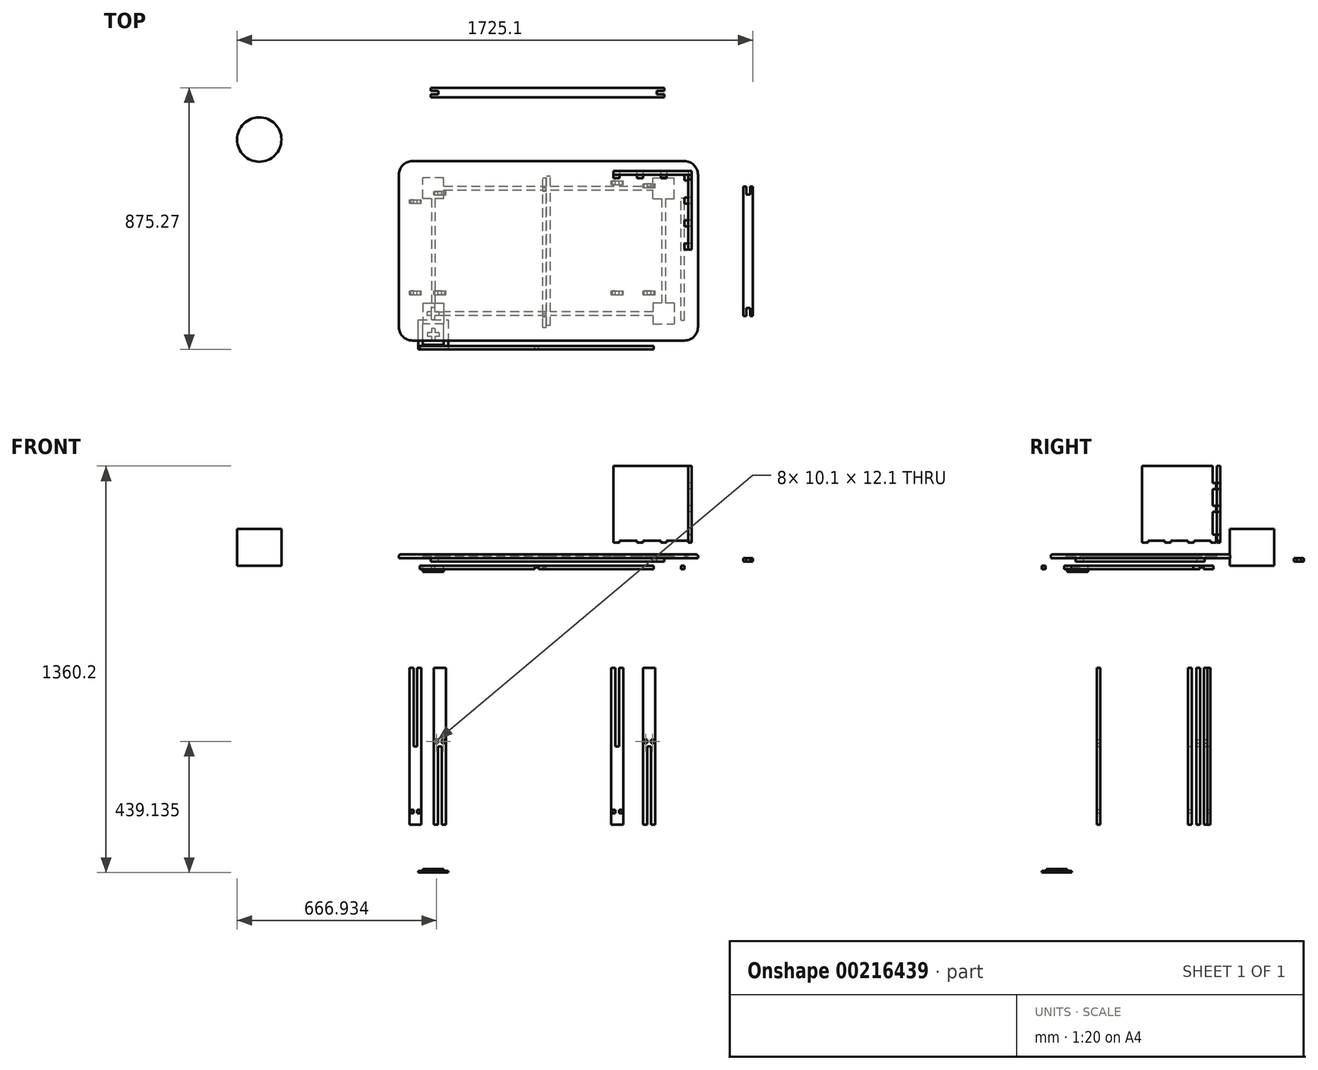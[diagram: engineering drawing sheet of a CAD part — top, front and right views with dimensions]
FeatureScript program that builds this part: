
annotation { "Feature Type Name" : "Feature", "Feature Type Description" : "" }
export const myFeature = defineFeature(function(context is Context, id is Id, definition is map)
    precondition{}
    {
        {
            var Q0;
            Q0=qCreatedBy(makeId("Top.planeOp"),FACE);
            var sketch = newSketch(context, id + "F0", { "sketchPlane" : qUnion([Q0])});
            skLineSegment(sketch, "E0.bottom", {"start": v(-704.37, 434.25) * mm, "end": v(295.63, 434.25) * mm});
            skLineSegment(sketch, "E0.top", {"start": v(-704.37, -165.75) * mm, "end": v(295.63, -165.75) * mm});
            skLineSegment(sketch, "E0.left", {"start": v(-704.37, 434.25) * mm, "end": v(-704.37, -165.75) * mm});
            skLineSegment(sketch, "E0.right", {"start": v(295.63, 434.25) * mm, "end": v(295.63, -165.75) * mm});
            skSolve(sketch);
        }
        {
            var Q0;
            Q0=makeQuery(id+"F0.imprint","IMPRINT",FACE,{"disambiguationData":[TD([[makeQuery(id+"F0.imprint","IMPRINT",EDGE,{"derivedFrom":sQuery(id+"F0.wireOp",EDGE,"E0.bottom")}),-1.0]])]});
            extrude(context, id + "F1", {"entities" : qUnion([Q0]), "depth" : 12 * mm});
        }
        {
            var Q0;
            Q0=makeQuery(id+"F1.opExtrude","CAP_EDGE",EDGE,{"disambiguationData":[OSD([sQuery(id+"F0.wireOp",EDGE,"E0.top")])],"isStart":false});
            var Q1;
            Q1=makeQuery(id+"F1.opExtrude","CAP_EDGE",EDGE,{"disambiguationData":[OSD([sQuery(id+"F0.wireOp",EDGE,"E0.left")])],"isStart":false});
            var Q2;
            Q2=makeQuery(id+"F1.opExtrude","CAP_FACE",FACE,{"disambiguationData":[OSD([sQuery(id+"F0.wireOp",EDGE,"E0.bottom"),sQuery(id+"F0.wireOp",EDGE,"E0.top"),sQuery(id+"F0.wireOp",EDGE,"E0.left"),sQuery(id+"F0.wireOp",EDGE,"E0.right")])],"isStart":false});
            fillet(context, id + "F2", {"entities" : qUnion([Q0, Q1, Q2]), "radius" : 5 * mm, "tangentPropagation" : true, "allowEdgeOverflow" : false});
        }
        {
            var Q0;
            Q0=makeQuery(id+"F1.opExtrude","CAP_FACE",FACE,{"disambiguationData":[OSD([sQuery(id+"F0.wireOp",EDGE,"E0.bottom"),sQuery(id+"F0.wireOp",EDGE,"E0.top"),sQuery(id+"F0.wireOp",EDGE,"E0.left"),sQuery(id+"F0.wireOp",EDGE,"E0.right")])],"isStart":true});
            var sketch = newSketch(context, id + "F3", { "sketchPlane" : qUnion([Q0])});
            skLineSegment(sketch, "E1.0", {"start": v(-704.37, -434.25) * mm, "end": v(-704.37, -134.25) * mm});
            skLineSegment(sketch, "E2.0", {"start": v(-704.37, 165.75) * mm, "end": v(295.63, 165.75) * mm});
            skLineSegment(sketch, "E3.0", {"start": v(-704.37, -434.25) * mm, "end": v(295.63, -434.25) * mm});
            skLineSegment(sketch, "E4.0", {"start": v(295.63, -134.25) * mm, "end": v(295.63, 165.75) * mm});
            skPoint(sketch, "E5", {"position": v(-704.37, -134.25) * mm});
            skPoint(sketch, "E6", {"position": v(295.63, -134.25) * mm});
            skPoint(sketch, "E7.orphan", {"position": v(295.63, -434.25) * mm});
            skPoint(sketch, "E8", {"position": v(-704.37, -284.25) * mm});
            skPoint(sketch, "E9", {"position": v(295.63, 15.75) * mm});
            skLineSegment(sketch, "E10", {"start": v(-704.37, -134.25) * mm, "end": v(-704.37, 165.75) * mm});
            skLineSegment(sketch, "E11", {"start": v(295.63, -134.25) * mm, "end": v(295.63, -434.25) * mm});
            skPoint(sketch, "E12", {"position": v(-704.37, 15.75) * mm});
            skPoint(sketch, "E13", {"position": v(295.63, -284.25) * mm});
            skPoint(sketch, "E14", {"position": v(-554.37, 40.75) * mm});
            skPoint(sketch, "E15", {"position": v(-554.37, -309.25) * mm});
            skLineSegment(sketch, "E16", {"start": v(-204.37, 15.75) * mm, "end": v(-204.37, -279) * mm, "construction": true});
            skPoint(sketch, "E17.MirrorP", {"position": v(145.63, 40.75) * mm});
            skPoint(sketch, "E18.MirrorP", {"position": v(145.63, -309.25) * mm});
            skLineSegment(sketch, "E19.bottom", {"start": v(-554.37, -309.25) * mm, "end": v(-624.37, -309.25) * mm});
            skLineSegment(sketch, "E19.top", {"start": v(-554.37, -379.25) * mm, "end": v(-624.37, -379.25) * mm});
            skLineSegment(sketch, "E19.left", {"start": v(-554.37, -309.25) * mm, "end": v(-554.37, -379.25) * mm});
            skLineSegment(sketch, "E19.right", {"start": v(-624.37, -309.25) * mm, "end": v(-624.37, -379.25) * mm});
            skLineSegment(sketch, "E20.top", {"start": v(-554.37, 110.75) * mm, "end": v(-624.37, 110.75) * mm});
            skLineSegment(sketch, "E20.left", {"start": v(-554.37, 40.75) * mm, "end": v(-554.37, 110.75) * mm});
            skLineSegment(sketch, "E20.right", {"start": v(-624.37, 40.75) * mm, "end": v(-624.37, 110.75) * mm});
            skLineSegment(sketch, "E21.MirrorCS", {"start": v(145.63, 40.75) * mm, "end": v(145.63, 110.75) * mm});
            skLineSegment(sketch, "E22.MirrorCS", {"start": v(145.63, 110.75) * mm, "end": v(215.63, 110.75) * mm});
            skLineSegment(sketch, "E23.MirrorCS", {"start": v(215.63, 40.75) * mm, "end": v(215.63, 110.75) * mm});
            skLineSegment(sketch, "E24", {"start": v(-624.37, 40.75) * mm, "end": v(-554.37, 40.75) * mm});
            skLineSegment(sketch, "E25.MirrorCS", {"start": v(215.63, 40.75) * mm, "end": v(145.63, 40.75) * mm});
            skLineSegment(sketch, "E26.MirrorCS", {"start": v(215.63, -309.25) * mm, "end": v(215.63, -379.25) * mm});
            skLineSegment(sketch, "E27.MirrorCS", {"start": v(145.63, -309.25) * mm, "end": v(145.63, -379.25) * mm});
            skLineSegment(sketch, "E28.MirrorCS", {"start": v(145.63, -379.25) * mm, "end": v(215.63, -379.25) * mm});
            skPoint(sketch, "E29.MirrorCS.start.orphan", {"position": v(215.63, -309.25) * mm});
            skLineSegment(sketch, "E30", {"start": v(145.63, -309.25) * mm, "end": v(215.63, -309.25) * mm});
            skSolve(sketch);
        }
        {
            var Q0;
            Q0=makeQuery(id+"F3.imprint","IMPRINT",FACE,{"disambiguationData":[TD([[makeQuery(id+"F3.imprint","IMPRINT",EDGE,{"derivedFrom":sQuery(id+"F3.wireOp",EDGE,"E20.top")}),1.0]])]});
            var Q1;
            Q1=makeQuery(id+"F3.imprint","IMPRINT",FACE,{"disambiguationData":[TD([[makeQuery(id+"F3.imprint","IMPRINT",EDGE,{"derivedFrom":sQuery(id+"F3.wireOp",EDGE,"E19.bottom")}),1.0]])]});
            var Q2;
            Q2=makeQuery(id+"F3.imprint","IMPRINT",FACE,{"disambiguationData":[TD([[makeQuery(id+"F3.imprint","IMPRINT",EDGE,{"derivedFrom":sQuery(id+"F3.wireOp",EDGE,"E26.MirrorCS")}),-1.0]])]});
            var Q3;
            Q3=makeQuery(id+"F3.imprint","IMPRINT",FACE,{"disambiguationData":[TD([[makeQuery(id+"F3.imprint","IMPRINT",EDGE,{"derivedFrom":sQuery(id+"F3.wireOp",EDGE,"E21.MirrorCS")}),-1.0]])]});
            extrude(context, id + "F4", {"entities" : qUnion([Q0, Q1, Q2, Q3]), "operationType" : NewBodyOperationType.REMOVE, "oppositeDirection" : true, "depth" : 6 * mm});
        }
        {
            var Q0;
            Q0=makeQuery(id+"F1.opExtrude","CAP_FACE",FACE,{"disambiguationData":[OSD([sQuery(id+"F0.wireOp",EDGE,"E0.bottom"),sQuery(id+"F0.wireOp",EDGE,"E0.top"),sQuery(id+"F0.wireOp",EDGE,"E0.left"),sQuery(id+"F0.wireOp",EDGE,"E0.right")])],"isStart":true});
            cPlane(context, id + "F5", {"entities" : qUnion([Q0]), "cplaneType" : CPlaneType.OFFSET, "offset" : 25 * mm, "width" : 150 * mm, "height" : 150 * mm});
        }
        {
            var Q0;
            Q0=qCreatedBy(id+"F5.planeOp",FACE);
            var sketch = newSketch(context, id + "F6", { "sketchPlane" : qUnion([Q0])});
            skLineSegment(sketch, "E31.0", {"start": v(-554.37, 40.75) * mm, "end": v(-554.37, 110.75) * mm});
            skLineSegment(sketch, "E32.0", {"start": v(-554.37, 110.75) * mm, "end": v(-624.37, 110.75) * mm});
            skLineSegment(sketch, "E33.0", {"start": v(-624.37, 40.75) * mm, "end": v(-624.37, 110.75) * mm});
            skLineSegment(sketch, "E34.0", {"start": v(-624.37, 40.75) * mm, "end": v(-554.37, 40.75) * mm});
            skPoint(sketch, "E35", {"position": v(-554.37, 75.75) * mm});
            skPoint(sketch, "E36", {"position": v(-589.37, 40.75) * mm});
            skPoint(sketch, "E37", {"position": v(-589.37, 75.75) * mm});
            skLineSegment(sketch, "E38", {"start": v(-599.37, 75.75) * mm, "end": v(-579.37, 75.75) * mm});
            skSolve(sketch);
        }
        {
            var Q0;
            Q0=makeQuery(id+"F6.imprint","IMPRINT",FACE,{"disambiguationData":[TD([[makeQuery(id+"F6.imprint","IMPRINT",EDGE,{"derivedFrom":sQuery(id+"F6.wireOp",EDGE,"E31.0")}),1.0]])]});
            extrude(context, id + "F7", {"entities" : qUnion([Q0]), "depth" : 20.8 * mm});
        }
        {
            var Q0;
            Q0=makeQuery(id+"F7.opExtrude","CAP_FACE",FACE,{"disambiguationData":[OSD([sQuery(id+"F6.wireOp",EDGE,"E31.0"),sQuery(id+"F6.wireOp",EDGE,"E32.0"),sQuery(id+"F6.wireOp",EDGE,"E33.0"),sQuery(id+"F6.wireOp",EDGE,"E34.0")])],"isStart":true});
            var sketch = newSketch(context, id + "F8", { "sketchPlane" : qUnion([Q0])});
            skPoint(sketch, "E39", {"position": v(-589.37, -40.75) * mm});
            skPoint(sketch, "E40", {"position": v(-554.37, -75.75) * mm});
            skPoint(sketch, "E41", {"position": v(-589.37, -75.75) * mm});
            skLineSegment(sketch, "E42", {"start": v(-589.37, -75.75) * mm, "end": v(-583.37, -75.75) * mm, "construction": true});
            skLineSegment(sketch, "E43.bottom", {"start": v(-583.37, -69.75) * mm, "end": v(-554.37, -69.75) * mm});
            skLineSegment(sketch, "E43.top", {"start": v(-583.37, -81.75) * mm, "end": v(-554.37, -81.75) * mm});
            skLineSegment(sketch, "E43.left", {"start": v(-589.37, -69.75) * mm, "end": v(-589.37, -81.75) * mm, "construction": true});
            skLineSegment(sketch, "E43.right", {"start": v(-554.37, -69.75) * mm, "end": v(-554.37, -81.75) * mm});
            skLineSegment(sketch, "E44.right", {"start": v(-624.37, -69.75) * mm, "end": v(-624.37, -81.75) * mm});
            skLineSegment(sketch, "E45.bottom", {"start": v(-595.37, -75.75) * mm, "end": v(-583.37, -75.75) * mm, "construction": true});
            skLineSegment(sketch, "E45.top", {"start": v(-595.37, -40.75) * mm, "end": v(-583.37, -40.75) * mm});
            skLineSegment(sketch, "E45.left", {"start": v(-595.37, -69.75) * mm, "end": v(-595.37, -40.75) * mm});
            skLineSegment(sketch, "E45.right", {"start": v(-583.37, -69.75) * mm, "end": v(-583.37, -40.75) * mm});
            skLineSegment(sketch, "E46.bottom", {"start": v(-583.37, -75.75) * mm, "end": v(-595.37, -75.75) * mm, "construction": true});
            skLineSegment(sketch, "E46.top", {"start": v(-583.37, -110.75) * mm, "end": v(-595.37, -110.75) * mm});
            skPoint(sketch, "E47.end.orphan", {"position": v(-589.37, -81.75) * mm});
            skLineSegment(sketch, "E48", {"start": v(-583.37, -81.75) * mm, "end": v(-595.37, -81.75) * mm});
            skLineSegment(sketch, "E49", {"start": v(-595.37, -69.75) * mm, "end": v(-595.37, -81.75) * mm});
            skSolve(sketch);
        }
        {
            var Q0;
            Q0=makeQuery(id+"F8.imprint","IMPRINT",FACE,{"disambiguationData":[TD([[makeQuery(id+"F8.imprint","IMPRINT",EDGE,{"derivedFrom":sQuery(id+"F8.wireOp",EDGE,"E43.bottom")}),-1.0]])]});
            extrude(context, id + "F9", {"entities" : qUnion([Q0]), "operationType" : NewBodyOperationType.REMOVE, "oppositeDirection" : true, "depth" : 12 * mm});
        }
        {
            var Q0;
            Q0=qCreatedBy(makeId("Front.planeOp"),FACE);
            var sketch = newSketch(context, id + "F10", { "sketchPlane" : qUnion([Q0])});
            skLineSegment(sketch, "E50.bottom", {"start": v(-669.23, -367.02) * mm, "end": v(-629.23, -367.02) * mm});
            skLineSegment(sketch, "E50.top", {"start": v(-669.23, -892.02) * mm, "end": v(-629.23, -892.02) * mm});
            skLineSegment(sketch, "E50.left", {"start": v(-669.23, -367.02) * mm, "end": v(-669.23, -892.02) * mm});
            skLineSegment(sketch, "E50.right", {"start": v(-629.23, -367.02) * mm, "end": v(-629.23, -892.02) * mm});
            skLineSegment(sketch, "E51.bottom", {"start": v(-587.48, -367.02) * mm, "end": v(-547.48, -367.02) * mm});
            skLineSegment(sketch, "E51.top", {"start": v(-587.48, -892.02) * mm, "end": v(-547.48, -892.02) * mm});
            skLineSegment(sketch, "E51.left", {"start": v(-587.48, -367.02) * mm, "end": v(-587.48, -892.02) * mm});
            skLineSegment(sketch, "E51.right", {"start": v(-547.48, -367.02) * mm, "end": v(-547.48, -892.02) * mm});
            skPoint(sketch, "E52", {"position": v(-655.28, -367.02) * mm});
            skPoint(sketch, "E53", {"position": v(-643.18, -367.02) * mm});
            skLineSegment(sketch, "E54.bottom", {"start": v(-655.28, -367.02) * mm, "end": v(-643.18, -367.02) * mm});
            skLineSegment(sketch, "E54.top", {"start": v(-655.28, -629.52) * mm, "end": v(-643.18, -629.52) * mm});
            skLineSegment(sketch, "E54.left", {"start": v(-655.28, -367.02) * mm, "end": v(-655.28, -629.52) * mm});
            skLineSegment(sketch, "E54.right", {"start": v(-643.18, -367.02) * mm, "end": v(-643.18, -629.52) * mm});
            skPoint(sketch, "E55", {"position": v(-573.53, -892.02) * mm});
            skPoint(sketch, "E56", {"position": v(-561.43, -892.02) * mm});
            skPoint(sketch, "E57.oppositeSnap0", {"position": v(-629.23, -629.52) * mm});
            skLineSegment(sketch, "E57.bottom", {"start": v(-561.43, -892.02) * mm, "end": v(-573.53, -892.02) * mm});
            skLineSegment(sketch, "E57.top", {"start": v(-561.43, -629.52) * mm, "end": v(-573.53, -629.52) * mm});
            skLineSegment(sketch, "E57.left", {"start": v(-561.43, -892.02) * mm, "end": v(-561.43, -629.52) * mm});
            skLineSegment(sketch, "E57.right", {"start": v(-573.53, -892.02) * mm, "end": v(-573.53, -629.52) * mm});
            skLineSegment(sketch, "E58", {"start": v(-567.48, -629.52) * mm, "end": v(-567.48, -367.02) * mm, "construction": true});
            skLineSegment(sketch, "E59", {"start": v(-649.23, -629.52) * mm, "end": v(-649.23, -892.02) * mm, "construction": true});
            skSolve(sketch);
        }
        {
            var Q0;
            Q0=makeQuery(id+"F7.opExtrude","CAP_FACE",FACE,{"disambiguationData":[OSD([sQuery(id+"F6.wireOp",EDGE,"E31.0"),sQuery(id+"F6.wireOp",EDGE,"E32.0"),sQuery(id+"F6.wireOp",EDGE,"E33.0"),sQuery(id+"F6.wireOp",EDGE,"E34.0")])],"isStart":false});
            var sketch = newSketch(context, id + "F11", { "sketchPlane" : qUnion([Q0])});
            skLineSegment(sketch, "E60.0.0", {"start": v(-624.37, 110.75) * mm, "end": v(-624.37, 40.75) * mm});
            skLineSegment(sketch, "E60.0.1", {"start": v(-624.37, 40.75) * mm, "end": v(-554.37, 40.75) * mm});
            skLineSegment(sketch, "E60.0.2", {"start": v(-554.37, 40.75) * mm, "end": v(-554.37, 110.75) * mm});
            skLineSegment(sketch, "E60.0.3", {"start": v(-554.37, 110.75) * mm, "end": v(-624.37, 110.75) * mm});
            skPoint(sketch, "E61", {"position": v(-569.37, 110.75) * mm});
            skPoint(sketch, "E62", {"position": v(-609.37, 110.75) * mm});
            skPoint(sketch, "E63", {"position": v(-554.37, 95.75) * mm});
            skPoint(sketch, "E64", {"position": v(-554.37, 55.75) * mm});
            skLineSegment(sketch, "E65.bottom", {"start": v(-583.27, 95.75) * mm, "end": v(-595.47, 95.75) * mm});
            skLineSegment(sketch, "E65.top", {"start": v(-583.27, 55.75) * mm, "end": v(-595.47, 55.75) * mm});
            skLineSegment(sketch, "E65.left", {"start": v(-554.37, 95.75) * mm, "end": v(-554.37, 55.75) * mm});
            skLineSegment(sketch, "E65.right", {"start": v(-609.37, 81.85) * mm, "end": v(-609.37, 69.65) * mm});
            skLineSegment(sketch, "E66.bottom", {"start": v(-569.37, 110.75) * mm, "end": v(-609.37, 110.75) * mm});
            skLineSegment(sketch, "E66.left", {"start": v(-569.37, 81.85) * mm, "end": v(-569.37, 69.65) * mm});
            skPoint(sketch, "E67", {"position": v(-554.37, 81.85) * mm});
            skPoint(sketch, "E68", {"position": v(-554.37, 69.65) * mm});
            skLineSegment(sketch, "E69.bottom", {"start": v(-569.37, 81.85) * mm, "end": v(-583.27, 81.85) * mm});
            skLineSegment(sketch, "E69.top", {"start": v(-569.37, 69.65) * mm, "end": v(-583.27, 69.65) * mm});
            skPoint(sketch, "E70", {"position": v(-583.27, 110.75) * mm});
            skPoint(sketch, "E71", {"position": v(-595.47, 110.75) * mm});
            skLineSegment(sketch, "E72.bottom", {"start": v(-595.47, 95.75) * mm, "end": v(-583.27, 95.75) * mm});
            skLineSegment(sketch, "E72.top", {"start": v(-595.47, 55.75) * mm, "end": v(-583.27, 55.75) * mm});
            skLineSegment(sketch, "E72.left", {"start": v(-595.47, 95.75) * mm, "end": v(-595.47, 81.85) * mm});
            skLineSegment(sketch, "E72.right", {"start": v(-583.27, 95.75) * mm, "end": v(-583.27, 81.85) * mm});
            skPoint(sketch, "E73.orphan", {"position": v(-609.37, 55.75) * mm});
            skLineSegment(sketch, "E74.trimOffspring", {"start": v(-595.47, 81.85) * mm, "end": v(-609.37, 81.85) * mm});
            skLineSegment(sketch, "E75.trimOffspring", {"start": v(-595.47, 69.65) * mm, "end": v(-595.47, 55.75) * mm});
            skLineSegment(sketch, "E76.trimOffspring", {"start": v(-583.27, 69.65) * mm, "end": v(-583.27, 55.75) * mm});
            skLineSegment(sketch, "E77.trimOffspring", {"start": v(-595.47, 69.65) * mm, "end": v(-609.37, 69.65) * mm});
            skSolve(sketch);
        }
        {
            var Q0;
            {var subQ5=sQuery(id+"F11.wireOp",EDGE,"E72.bottom");Q0=makeQuery(id+"F11.imprint","IMPRINT",FACE,{"disambiguationData":[TD([[makeQuery(id+"F11.imprint","IMPRINT",EDGE,{"derivedFrom":subQ5}),-1.0]])]});}
            var Q1;
            {var subQ0=sQuery(id+"F11.wireOp",EDGE,"E72.right");var subQ1=sQuery(id+"F11.wireOp",EDGE,"E69.bottom");var subQ2=makeQuery(id+"F11.imprint","INTERSECT",VERTEX,{"derivedFrom":[subQ1,subQ0]});Q1=makeQuery(id+"F11.imprint","IMPRINT",FACE,{"disambiguationData":[TD([[makeQuery(id+"F11.imprint","IMPRINT",EDGE,{"disambiguationData":[TD([[subQ2,-1.0]])],"derivedFrom":subQ1}),1.0]])]});}
            var Q2;
            {var subQ0=sQuery(id+"F11.wireOp",EDGE,"E65.right");Q2=makeQuery(id+"F11.imprint","IMPRINT",FACE,{"disambiguationData":[TD([[makeQuery(id+"F11.imprint","IMPRINT",EDGE,{"derivedFrom":subQ0}),1.0]])]});}
            var Q3;
            {var subQ0=sQuery(id+"F11.wireOp",EDGE,"E66.left");Q3=makeQuery(id+"F11.imprint","IMPRINT",FACE,{"disambiguationData":[TD([[makeQuery(id+"F11.imprint","IMPRINT",EDGE,{"derivedFrom":subQ0}),-1.0]])]});}
            var Q4;
            {var subQ5=sQuery(id+"F11.wireOp",EDGE,"E72.top");Q4=makeQuery(id+"F11.imprint","IMPRINT",FACE,{"disambiguationData":[TD([[makeQuery(id+"F11.imprint","IMPRINT",EDGE,{"derivedFrom":subQ5}),1.0]])]});}
            extrude(context, id + "F12", {"entities" : qUnion([Q0, Q1, Q2, Q3, Q4]), "operationType" : NewBodyOperationType.REMOVE, "oppositeDirection" : true, "depth" : 8 * mm});
        }
        {
            var Q0;
            Q0=makeQuery(id+"F10.imprint","IMPRINT",FACE,{"disambiguationData":[TD([[makeQuery(id+"F10.imprint","IMPRINT",EDGE,{"derivedFrom":sQuery(id+"F10.wireOp",EDGE,"E50.top")}),1.0]])]});
            var Q1;
            Q1=makeQuery(id+"F10.imprint","IMPRINT",FACE,{"disambiguationData":[TD([[makeQuery(id+"F10.imprint","IMPRINT",EDGE,{"derivedFrom":sQuery(id+"F10.wireOp",EDGE,"E51.bottom")}),-1.0]])]});
            extrude(context, id + "F13", {"entities" : qUnion([Q0, Q1]), "depth" : 12 * mm});
        }
        {
            var Q0;
            Q0=makeQuery(id+"F13.opExtrude","SWEPT_BODY",BODY,{"disambiguationData":[OSD([sQuery(id+"F10.wireOp",EDGE,"E50.bottom"),sQuery(id+"F10.wireOp",EDGE,"E50.top"),sQuery(id+"F10.wireOp",EDGE,"E50.left"),sQuery(id+"F10.wireOp",EDGE,"E50.right"),sQuery(id+"F10.wireOp",EDGE,"E54.top"),sQuery(id+"F10.wireOp",EDGE,"E54.left"),sQuery(id+"F10.wireOp",EDGE,"E54.right")])]});
            transform(context, id + "F14", {"entities" : qUnion([Q0]), "transformType" : TransformType.TRANSLATION_3D, "dx" : 675 * mm, "dy" : 0 * mm, "dz" : 0 * mm, "makeCopy" : true});
        }
        {
            var Q0;
            Q0=makeQuery(id+"F13.opExtrude","SWEPT_BODY",BODY,{"disambiguationData":[OSD([sQuery(id+"F10.wireOp",EDGE,"E51.bottom"),sQuery(id+"F10.wireOp",EDGE,"E51.top"),sQuery(id+"F10.wireOp",EDGE,"E51.left"),sQuery(id+"F10.wireOp",EDGE,"E51.right"),sQuery(id+"F10.wireOp",EDGE,"E57.top"),sQuery(id+"F10.wireOp",EDGE,"E57.left"),sQuery(id+"F10.wireOp",EDGE,"E57.right")])]});
            transform(context, id + "F15", {"entities" : qUnion([Q0]), "transformType" : TransformType.TRANSLATION_3D, "dx" : 700 * mm, "dy" : 0 * mm, "dz" : 0 * mm, "makeCopy" : true});
        }
        {
            var Q0;
            Q0=makeQuery(id+"F13.opExtrude","CAP_FACE",FACE,{"disambiguationData":[OSD([sQuery(id+"F10.wireOp",EDGE,"E50.bottom"),sQuery(id+"F10.wireOp",EDGE,"E50.top"),sQuery(id+"F10.wireOp",EDGE,"E50.left"),sQuery(id+"F10.wireOp",EDGE,"E50.right"),sQuery(id+"F10.wireOp",EDGE,"E54.top"),sQuery(id+"F10.wireOp",EDGE,"E54.left"),sQuery(id+"F10.wireOp",EDGE,"E54.right")])],"isStart":false});
            var sketch = newSketch(context, id + "F16", { "sketchPlane" : qUnion([Q0])});
            skLineSegment(sketch, "E78.0.0", {"start": v(-655.28, -367.02) * mm, "end": v(-669.23, -367.02) * mm});
            skLineSegment(sketch, "E78.0.1", {"start": v(-669.23, -367.02) * mm, "end": v(-669.23, -892.02) * mm});
            skLineSegment(sketch, "E78.0.2", {"start": v(-669.23, -892.02) * mm, "end": v(-629.23, -892.02) * mm});
            skLineSegment(sketch, "E78.0.3", {"start": v(-629.23, -892.02) * mm, "end": v(-629.23, -367.02) * mm});
            skLineSegment(sketch, "E78.0.4", {"start": v(-629.23, -367.02) * mm, "end": v(-643.18, -367.02) * mm});
            skLineSegment(sketch, "E78.0.5", {"start": v(-643.18, -367.02) * mm, "end": v(-643.18, -629.52) * mm});
            skLineSegment(sketch, "E78.0.6", {"start": v(-643.18, -629.52) * mm, "end": v(-655.28, -629.52) * mm});
            skLineSegment(sketch, "E78.0.7", {"start": v(-655.28, -629.52) * mm, "end": v(-655.28, -367.02) * mm});
            skPoint(sketch, "E79", {"position": v(-629.23, -842.02) * mm});
            skLineSegment(sketch, "E80.bottom", {"start": v(-643.18, -629.52) * mm, "end": v(-655.28, -629.52) * mm, "construction": true});
            skLineSegment(sketch, "E80.top", {"start": v(-643.18, -877.56) * mm, "end": v(-655.28, -877.56) * mm, "construction": true});
            skLineSegment(sketch, "E80.left", {"start": v(-643.18, -629.52) * mm, "end": v(-643.18, -842.02) * mm, "construction": true});
            skLineSegment(sketch, "E80.right", {"start": v(-655.28, -629.52) * mm, "end": v(-655.28, -842.02) * mm, "construction": true});
            skLineSegment(sketch, "E81.bottom", {"start": v(-643.18, -842.02) * mm, "end": v(-633.18, -842.02) * mm});
            skLineSegment(sketch, "E81.top", {"start": v(-643.18, -854.12) * mm, "end": v(-633.18, -854.12) * mm});
            skLineSegment(sketch, "E81.right", {"start": v(-633.18, -842.02) * mm, "end": v(-633.18, -854.12) * mm});
            skPoint(sketch, "E82", {"position": v(-649.23, -877.56) * mm});
            skLineSegment(sketch, "E83", {"start": v(-649.23, -877.56) * mm, "end": v(-649.23, -841.02) * mm, "construction": true});
            skLineSegment(sketch, "E84.MirrorCS", {"start": v(-655.28, -854.12) * mm, "end": v(-665.28, -854.12) * mm});
            skLineSegment(sketch, "E85.MirrorCS", {"start": v(-665.28, -842.02) * mm, "end": v(-665.28, -854.12) * mm});
            skLineSegment(sketch, "E86.MirrorCS", {"start": v(-655.28, -842.02) * mm, "end": v(-665.28, -842.02) * mm});
            skLineSegment(sketch, "E87.trimOffspring", {"start": v(-643.18, -854.12) * mm, "end": v(-643.18, -877.56) * mm, "construction": true});
            skLineSegment(sketch, "E88.trimOffspring", {"start": v(-655.28, -854.12) * mm, "end": v(-655.28, -877.56) * mm, "construction": true});
            skLineSegment(sketch, "E89", {"start": v(-643.18, -854.12) * mm, "end": v(-643.18, -842.02) * mm});
            skLineSegment(sketch, "E90", {"start": v(-655.28, -854.12) * mm, "end": v(-655.28, -842.02) * mm});
            skLineSegment(sketch, "E91.0.0", {"start": v(19.72, -367.02) * mm, "end": v(5.77, -367.02) * mm});
            skLineSegment(sketch, "E91.0.1", {"start": v(5.77, -367.02) * mm, "end": v(5.77, -892.02) * mm});
            skLineSegment(sketch, "E91.0.2", {"start": v(5.77, -892.02) * mm, "end": v(45.77, -892.02) * mm});
            skLineSegment(sketch, "E91.0.3", {"start": v(45.77, -892.02) * mm, "end": v(45.77, -367.02) * mm});
            skLineSegment(sketch, "E91.0.4", {"start": v(45.77, -367.02) * mm, "end": v(31.82, -367.02) * mm});
            skLineSegment(sketch, "E91.0.5", {"start": v(31.82, -367.02) * mm, "end": v(31.82, -629.52) * mm});
            skLineSegment(sketch, "E91.0.6", {"start": v(31.82, -629.52) * mm, "end": v(19.72, -629.52) * mm});
            skLineSegment(sketch, "E91.0.7", {"start": v(19.72, -629.52) * mm, "end": v(19.72, -367.02) * mm});
            skLineSegment(sketch, "E92", {"start": v(-629.23, -892.02) * mm, "end": v(5.77, -892.02) * mm, "construction": true});
            skPoint(sketch, "E93", {"position": v(-311.73, -892.02) * mm});
            skLineSegment(sketch, "E94", {"start": v(-311.73, -892.02) * mm, "end": v(-311.73, -731.08) * mm, "construction": true});
            skLineSegment(sketch, "E95.MirrorCS", {"start": v(19.72, -854.12) * mm, "end": v(9.72, -854.12) * mm});
            skLineSegment(sketch, "E96.MirrorCS", {"start": v(19.72, -854.12) * mm, "end": v(19.72, -842.02) * mm});
            skLineSegment(sketch, "E97.MirrorCS", {"start": v(19.72, -842.02) * mm, "end": v(9.72, -842.02) * mm});
            skLineSegment(sketch, "E98.MirrorCS", {"start": v(9.72, -842.02) * mm, "end": v(9.72, -854.12) * mm});
            skLineSegment(sketch, "E99.MirrorCS", {"start": v(31.82, -842.02) * mm, "end": v(41.82, -842.02) * mm});
            skLineSegment(sketch, "E100.MirrorCS", {"start": v(31.82, -854.12) * mm, "end": v(31.82, -842.02) * mm});
            skLineSegment(sketch, "E101.MirrorCS", {"start": v(31.82, -854.12) * mm, "end": v(41.82, -854.12) * mm});
            skLineSegment(sketch, "E102.MirrorCS", {"start": v(41.82, -842.02) * mm, "end": v(41.82, -854.12) * mm});
            skSolve(sketch);
        }
        {
            var Q0;
            Q0=makeQuery(id+"F16.imprint","IMPRINT",FACE,{"disambiguationData":[TD([[makeQuery(id+"F16.imprint","IMPRINT",EDGE,{"derivedFrom":sQuery(id+"F16.wireOp",EDGE,"E84.MirrorCS")}),-1.0]])]});
            var Q1;
            Q1=makeQuery(id+"F16.imprint","IMPRINT",FACE,{"disambiguationData":[TD([[makeQuery(id+"F16.imprint","IMPRINT",EDGE,{"derivedFrom":sQuery(id+"F16.wireOp",EDGE,"E81.bottom")}),-1.0]])]});
            var Q2;
            Q2=makeQuery(id+"F16.imprint","IMPRINT",FACE,{"disambiguationData":[TD([[makeQuery(id+"F16.imprint","IMPRINT",EDGE,{"derivedFrom":sQuery(id+"F16.wireOp",EDGE,"E95.MirrorCS")}),-1.0]])]});
            var Q3;
            Q3=makeQuery(id+"F16.imprint","IMPRINT",FACE,{"disambiguationData":[TD([[makeQuery(id+"F16.imprint","IMPRINT",EDGE,{"derivedFrom":sQuery(id+"F16.wireOp",EDGE,"E99.MirrorCS")}),-1.0]])]});
            extrude(context, id + "F17", {"entities" : qUnion([Q0, Q1, Q2, Q3]), "operationType" : NewBodyOperationType.REMOVE, "oppositeDirection" : true, "depth" : 25 * mm});
        }
        {
            var Q0;
            Q0=makeQuery(id+"F15.opPattern","COPY",FACE,{"derivedFrom":makeQuery(id+"F13.opExtrude","CAP_FACE",FACE,{"disambiguationData":[OSD([sQuery(id+"F10.wireOp",EDGE,"E51.bottom"),sQuery(id+"F10.wireOp",EDGE,"E51.top"),sQuery(id+"F10.wireOp",EDGE,"E51.left"),sQuery(id+"F10.wireOp",EDGE,"E51.right"),sQuery(id+"F10.wireOp",EDGE,"E57.top"),sQuery(id+"F10.wireOp",EDGE,"E57.left"),sQuery(id+"F10.wireOp",EDGE,"E57.right")])],"isStart":true}),"instanceName":"1"});
            var sketch = newSketch(context, id + "F18", { "sketchPlane" : qUnion([Q0])});
            skLineSegment(sketch, "E103.0.0", {"start": v(-138.57, -629.52) * mm, "end": v(-126.47, -629.52) * mm});
            skLineSegment(sketch, "E103.0.1", {"start": v(-126.47, -629.52) * mm, "end": v(-126.47, -892.02) * mm});
            skLineSegment(sketch, "E103.0.2", {"start": v(-126.47, -892.02) * mm, "end": v(-112.52, -892.02) * mm});
            skLineSegment(sketch, "E103.0.3", {"start": v(-112.52, -892.02) * mm, "end": v(-112.52, -367.02) * mm});
            skLineSegment(sketch, "E103.0.4", {"start": v(-112.52, -367.02) * mm, "end": v(-152.52, -367.02) * mm});
            skLineSegment(sketch, "E103.0.5", {"start": v(-152.52, -367.02) * mm, "end": v(-152.52, -892.02) * mm});
            skLineSegment(sketch, "E103.0.6", {"start": v(-152.52, -892.02) * mm, "end": v(-138.57, -892.02) * mm});
            skLineSegment(sketch, "E103.0.7", {"start": v(-138.57, -892.02) * mm, "end": v(-138.57, -629.52) * mm});
            skLineSegment(sketch, "E104.bottom", {"start": v(-126.47, -629.52) * mm, "end": v(-138.57, -629.52) * mm, "construction": true});
            skLineSegment(sketch, "E104.top", {"start": v(-126.47, -426.7) * mm, "end": v(-138.57, -426.7) * mm, "construction": true});
            skLineSegment(sketch, "E104.left", {"start": v(-126.47, -629.52) * mm, "end": v(-126.47, -619.12) * mm, "construction": true});
            skLineSegment(sketch, "E104.right", {"start": v(-138.57, -629.52) * mm, "end": v(-138.57, -619.12) * mm, "construction": true});
            skLineSegment(sketch, "E105.0.0", {"start": v(561.43, -629.52) * mm, "end": v(573.53, -629.52) * mm, "construction": true});
            skLineSegment(sketch, "E105.0.1", {"start": v(573.53, -629.52) * mm, "end": v(573.53, -892.02) * mm, "construction": true});
            skLineSegment(sketch, "E105.0.2", {"start": v(573.53, -892.02) * mm, "end": v(587.48, -892.02) * mm, "construction": true});
            skLineSegment(sketch, "E105.0.3", {"start": v(587.48, -892.02) * mm, "end": v(587.48, -367.02) * mm, "construction": true});
            skLineSegment(sketch, "E105.0.4", {"start": v(587.48, -367.02) * mm, "end": v(547.48, -367.02) * mm, "construction": true});
            skLineSegment(sketch, "E105.0.5", {"start": v(547.48, -367.02) * mm, "end": v(547.48, -892.02) * mm, "construction": true});
            skLineSegment(sketch, "E105.0.6", {"start": v(547.48, -892.02) * mm, "end": v(561.43, -892.02) * mm, "construction": true});
            skLineSegment(sketch, "E105.0.7", {"start": v(561.43, -892.02) * mm, "end": v(561.43, -629.52) * mm, "construction": true});
            skLineSegment(sketch, "E106.bottom", {"start": v(573.53, -629.52) * mm, "end": v(561.43, -629.52) * mm, "construction": true});
            skLineSegment(sketch, "E106.top", {"start": v(573.53, -388.02) * mm, "end": v(561.43, -388.02) * mm, "construction": true});
            skLineSegment(sketch, "E106.left", {"start": v(573.53, -629.52) * mm, "end": v(573.53, -388.02) * mm, "construction": true});
            skLineSegment(sketch, "E106.right", {"start": v(561.43, -629.52) * mm, "end": v(561.43, -388.02) * mm, "construction": true});
            skLineSegment(sketch, "E107", {"start": v(-112.52, -367.02) * mm, "end": v(547.48, -367.02) * mm, "construction": true});
            skLineSegment(sketch, "E108", {"start": v(217.48, -367.02) * mm, "end": v(217.48, -451.72) * mm, "construction": true});
            skLineSegment(sketch, "E109.bottom", {"start": v(-126.47, -619.12) * mm, "end": v(-116.37, -619.12) * mm});
            skLineSegment(sketch, "E109.top", {"start": v(-126.47, -607.02) * mm, "end": v(-116.37, -607.02) * mm});
            skLineSegment(sketch, "E109.right", {"start": v(-116.37, -619.12) * mm, "end": v(-116.37, -607.02) * mm});
            skLineSegment(sketch, "E110.bottom", {"start": v(-138.57, -607.02) * mm, "end": v(-148.67, -607.02) * mm});
            skLineSegment(sketch, "E110.top", {"start": v(-138.57, -619.12) * mm, "end": v(-148.67, -619.12) * mm});
            skLineSegment(sketch, "E110.right", {"start": v(-148.67, -607.02) * mm, "end": v(-148.67, -619.12) * mm});
            skLineSegment(sketch, "E111.trimOffspring", {"start": v(-126.47, -607.02) * mm, "end": v(-126.47, -426.7) * mm, "construction": true});
            skLineSegment(sketch, "E112.trimOffspring", {"start": v(-138.57, -607.02) * mm, "end": v(-138.57, -426.7) * mm, "construction": true});
            skLineSegment(sketch, "E113", {"start": v(-138.57, -607.02) * mm, "end": v(-138.57, -619.12) * mm});
            skLineSegment(sketch, "E114", {"start": v(-126.47, -619.12) * mm, "end": v(-126.47, -607.02) * mm});
            skLineSegment(sketch, "E115.MirrorCS", {"start": v(561.43, -607.02) * mm, "end": v(551.33, -607.02) * mm});
            skLineSegment(sketch, "E116.MirrorCS", {"start": v(561.43, -619.12) * mm, "end": v(561.43, -607.02) * mm});
            skLineSegment(sketch, "E117.MirrorCS", {"start": v(561.43, -619.12) * mm, "end": v(551.33, -619.12) * mm});
            skLineSegment(sketch, "E118.MirrorCS", {"start": v(551.33, -619.12) * mm, "end": v(551.33, -607.02) * mm});
            skLineSegment(sketch, "E119.MirrorCS", {"start": v(573.53, -619.12) * mm, "end": v(583.63, -619.12) * mm});
            skLineSegment(sketch, "E120.MirrorCS", {"start": v(573.53, -607.02) * mm, "end": v(573.53, -619.12) * mm});
            skLineSegment(sketch, "E121.MirrorCS", {"start": v(573.53, -607.02) * mm, "end": v(583.63, -607.02) * mm});
            skLineSegment(sketch, "E122.MirrorCS", {"start": v(583.63, -607.02) * mm, "end": v(583.63, -619.12) * mm});
            skSolve(sketch);
        }
        {
            var Q0;
            Q0=makeQuery(id+"F18.imprint","IMPRINT",FACE,{"disambiguationData":[TD([[makeQuery(id+"F18.imprint","IMPRINT",EDGE,{"derivedFrom":sQuery(id+"F18.wireOp",EDGE,"E109.bottom")}),1.0]])]});
            var Q1;
            Q1=makeQuery(id+"F18.imprint","IMPRINT",FACE,{"disambiguationData":[TD([[makeQuery(id+"F18.imprint","IMPRINT",EDGE,{"derivedFrom":sQuery(id+"F18.wireOp",EDGE,"E110.bottom")}),1.0]])]});
            var Q2;
            Q2=makeQuery(id+"F18.imprint","IMPRINT",FACE,{"disambiguationData":[TD([[makeQuery(id+"F18.imprint","IMPRINT",EDGE,{"derivedFrom":sQuery(id+"F18.wireOp",EDGE,"E115.MirrorCS")}),1.0]])]});
            var Q3;
            Q3=makeQuery(id+"F18.imprint","IMPRINT",FACE,{"disambiguationData":[TD([[makeQuery(id+"F18.imprint","IMPRINT",EDGE,{"derivedFrom":sQuery(id+"F18.wireOp",EDGE,"E119.MirrorCS")}),1.0]])]});
            extrude(context, id + "F19", {"entities" : qUnion([Q0, Q1, Q2, Q3]), "operationType" : NewBodyOperationType.REMOVE, "oppositeDirection" : true, "depth" : 25 * mm});
        }
        {
            var Q0;
            Q0=makeQuery(id+"F14.opPattern","COPY",BODY,{"derivedFrom":makeQuery(id+"F13.opExtrude","SWEPT_BODY",BODY,{"disambiguationData":[OSD([sQuery(id+"F10.wireOp",EDGE,"E50.bottom"),sQuery(id+"F10.wireOp",EDGE,"E50.top"),sQuery(id+"F10.wireOp",EDGE,"E50.left"),sQuery(id+"F10.wireOp",EDGE,"E50.right"),sQuery(id+"F10.wireOp",EDGE,"E54.top"),sQuery(id+"F10.wireOp",EDGE,"E54.left"),sQuery(id+"F10.wireOp",EDGE,"E54.right")])]}),"instanceName":"1"});
            transform(context, id + "F20", {"entities" : qUnion([Q0]), "transformType" : TransformType.TRANSLATION_3D, "dx" : 0 * mm, "dy" : 368 * mm, "dz" : 0 * mm, "makeCopy" : true});
        }
        {
            var Q0;
            Q0=makeQuery(id+"F15.opPattern","COPY",BODY,{"derivedFrom":makeQuery(id+"F13.opExtrude","SWEPT_BODY",BODY,{"disambiguationData":[OSD([sQuery(id+"F10.wireOp",EDGE,"E51.bottom"),sQuery(id+"F10.wireOp",EDGE,"E51.top"),sQuery(id+"F10.wireOp",EDGE,"E51.left"),sQuery(id+"F10.wireOp",EDGE,"E51.right"),sQuery(id+"F10.wireOp",EDGE,"E57.top"),sQuery(id+"F10.wireOp",EDGE,"E57.left"),sQuery(id+"F10.wireOp",EDGE,"E57.right")])]}),"instanceName":"1"});
            transform(context, id + "F21", {"entities" : qUnion([Q0]), "transformType" : TransformType.TRANSLATION_3D, "dx" : 0 * mm, "dy" : 358 * mm, "dz" : 0 * mm, "makeCopy" : true});
        }
        {
            var Q0;
            Q0=makeQuery(id+"F13.opExtrude","SWEPT_BODY",BODY,{"disambiguationData":[OSD([sQuery(id+"F10.wireOp",EDGE,"E50.bottom"),sQuery(id+"F10.wireOp",EDGE,"E50.top"),sQuery(id+"F10.wireOp",EDGE,"E50.left"),sQuery(id+"F10.wireOp",EDGE,"E50.right"),sQuery(id+"F10.wireOp",EDGE,"E54.top"),sQuery(id+"F10.wireOp",EDGE,"E54.left"),sQuery(id+"F10.wireOp",EDGE,"E54.right")])]});
            transform(context, id + "F22", {"entities" : qUnion([Q0]), "transformType" : TransformType.TRANSLATION_3D, "dx" : 0 * mm, "dy" : 305 * mm, "dz" : 0 * mm, "makeCopy" : true});
        }
        {
            var Q0;
            Q0=makeQuery(id+"F13.opExtrude","SWEPT_BODY",BODY,{"disambiguationData":[OSD([sQuery(id+"F10.wireOp",EDGE,"E51.bottom"),sQuery(id+"F10.wireOp",EDGE,"E51.top"),sQuery(id+"F10.wireOp",EDGE,"E51.left"),sQuery(id+"F10.wireOp",EDGE,"E51.right"),sQuery(id+"F10.wireOp",EDGE,"E57.top"),sQuery(id+"F10.wireOp",EDGE,"E57.left"),sQuery(id+"F10.wireOp",EDGE,"E57.right")])]});
            transform(context, id + "F23", {"entities" : qUnion([Q0]), "transformType" : TransformType.TRANSLATION_3D, "dx" : 0 * mm, "dy" : 333 * mm, "dz" : 0 * mm, "makeCopy" : true});
        }
        {
            var Q0;
            Q0=makeQuery(id+"F7.opExtrude","SWEPT_BODY",BODY,{"disambiguationData":[OSD([sQuery(id+"F6.wireOp",EDGE,"E31.0"),sQuery(id+"F6.wireOp",EDGE,"E32.0"),sQuery(id+"F6.wireOp",EDGE,"E33.0"),sQuery(id+"F6.wireOp",EDGE,"E34.0")])]});
            transform(context, id + "F24", {"entities" : qUnion([Q0]), "transformType" : TransformType.TRANSLATION_3D, "dx" : 0 * mm, "dy" : 0 * mm, "dz" : -1036 * mm, "makeCopy" : true});
        }
        {
            var Q0;
            Q0=makeQuery(id+"F24.opPattern","COPY",FACE,{"derivedFrom":makeQuery(id+"F9.boolean.opBoolean","COPY",FACE,{"derivedFrom":makeQuery(id+"F9.opExtrude","CAP_FACE",FACE,{"disambiguationData":[OSD([sQuery(id+"F8.wireOp",EDGE,"E43.bottom"),sQuery(id+"F8.wireOp",EDGE,"E43.top"),sQuery(id+"F8.wireOp",EDGE,"E43.right"),sQuery(id+"F8.wireOp",EDGE,"E44.bottom"),sQuery(id+"F8.wireOp",EDGE,"E44.top"),sQuery(id+"F8.wireOp",EDGE,"E44.right"),sQuery(id+"F8.wireOp",EDGE,"E45.top"),sQuery(id+"F8.wireOp",EDGE,"E45.left"),sQuery(id+"F8.wireOp",EDGE,"E45.right"),sQuery(id+"F8.wireOp",EDGE,"E46.top"),sQuery(id+"F8.wireOp",EDGE,"E46.left"),sQuery(id+"F8.wireOp",EDGE,"E46.right")])],"isStart":false})}),"instanceName":"1"});
            extrude(context, id + "F25", {"entities" : qUnion([Q0]), "operationType" : NewBodyOperationType.ADD, "depth" : 5 * mm});
        }
        {
            var Q0;
            Q0=makeQuery(id+"F24.opPattern","COPY",BODY,{"derivedFrom":makeQuery(id+"F7.opExtrude","SWEPT_BODY",BODY,{"disambiguationData":[OSD([sQuery(id+"F6.wireOp",EDGE,"E31.0"),sQuery(id+"F6.wireOp",EDGE,"E32.0"),sQuery(id+"F6.wireOp",EDGE,"E33.0"),sQuery(id+"F6.wireOp",EDGE,"E34.0")])]}),"instanceName":"1"});
            var Q1;
            {var subQ0=sQuery(id+"F6.wireOp",EDGE,"E33.0");var subQ1=sQuery(id+"F6.wireOp",EDGE,"E32.0");var subQ2=sQuery(id+"F6.wireOp",EDGE,"E31.0");var subQ5=makeQuery(id+"F7.opExtrude","CAP_EDGE",EDGE,{"disambiguationData":[OSD([subQ1])],"isStart":true});Q1=makeQuery(id+"F24.opPattern","COPY",EDGE,{"derivedFrom":makeQuery(id+"FutpuZrPhDoch6k_8.boolean.opBoolean","MERGE",EDGE,{"derivedFrom":[makeQuery(id+"F9.boolean.opBoolean","SPLIT",EDGE,{"disambiguationData":[TD([makeQuery(id+"F7.opExtrude","SWEPT_FACE",FACE,{"disambiguationData":[OSD([subQ2])]})])],"derivedFrom":subQ5}),makeQuery(id+"F9.boolean.opBoolean","SPLIT",EDGE,{"disambiguationData":[TD([makeQuery(id+"F7.opExtrude","SWEPT_FACE",FACE,{"disambiguationData":[OSD([subQ0])]})])],"derivedFrom":subQ5}),makeQuery(id+"FutpuZrPhDoch6k_8.opExtrude","CAP_EDGE",EDGE,{"disambiguationData":[OSD([sQuery(id+"FvpKIrItqQz19g1_8.wireOp",EDGE,"7xp0iT8u-hfBB-a3Bu-mP94-j6wXYNo7JhAX")])],"isStart":false})]}),"instanceName":"1"});}
            transform(context, id + "F26", {"entities" : qUnion([Q0]), "transformType" : TransformType.ROTATION, "transformAxis" : qUnion([Q1]), "angle" : 180 * degree, "makeCopy" : false});
        }
        {
            var Q0;
            Q0=makeQuery(id+"F1.opExtrude","CAP_FACE",FACE,{"disambiguationData":[OSD([sQuery(id+"F0.wireOp",EDGE,"E0.bottom"),sQuery(id+"F0.wireOp",EDGE,"E0.top"),sQuery(id+"F0.wireOp",EDGE,"E0.left"),sQuery(id+"F0.wireOp",EDGE,"E0.right")])],"isStart":true});
            var sketch = newSketch(context, id + "F27", { "sketchPlane" : qUnion([Q0])});
            skLineSegment(sketch, "E123.0", {"start": v(-595.37, 81.75) * mm, "end": v(-595.37, 40.75) * mm});
            skLineSegment(sketch, "E124.0", {"start": v(-554.37, 81.75) * mm, "end": v(-595.37, 81.75) * mm});
            skLineSegment(sketch, "E125.0", {"start": v(-583.37, 69.75) * mm, "end": v(-554.37, 69.75) * mm});
            skLineSegment(sketch, "E126.0", {"start": v(-583.37, 69.75) * mm, "end": v(-583.37, 40.75) * mm});
            skLineSegment(sketch, "E127", {"start": v(-554.37, -350.25) * mm, "end": v(-595.37, -350.25) * mm});
            skLineSegment(sketch, "E128", {"start": v(-595.37, -350.25) * mm, "end": v(-595.37, -309.25) * mm});
            skLineSegment(sketch, "E129", {"start": v(-554.37, -350.25) * mm, "end": v(-210.37, -350.25) * mm});
            skLineSegment(sketch, "E130", {"start": v(186.63, -350.25) * mm, "end": v(186.63, 81.75) * mm});
            skLineSegment(sketch, "E131", {"start": v(145.63, 81.75) * mm, "end": v(-198.37, 81.75) * mm});
            skLineSegment(sketch, "E132", {"start": v(-595.37, -309.25) * mm, "end": v(-595.37, 40.75) * mm});
            skLineSegment(sketch, "E133.0", {"start": v(145.63, 69.75) * mm, "end": v(-198.37, 69.75) * mm});
            skLineSegment(sketch, "E134.0", {"start": v(174.63, -338.25) * mm, "end": v(174.63, 69.75) * mm});
            skLineSegment(sketch, "E135.0", {"start": v(-554.37, -338.25) * mm, "end": v(-210.37, -338.25) * mm});
            skLineSegment(sketch, "E136.0", {"start": v(-583.37, -309.25) * mm, "end": v(-583.37, 40.75) * mm});
            skLineSegment(sketch, "E137", {"start": v(-583.37, -309.25) * mm, "end": v(-583.37, -338.25) * mm});
            skLineSegment(sketch, "E138", {"start": v(-583.37, -338.25) * mm, "end": v(-554.37, -338.25) * mm});
            skLineSegment(sketch, "E139.0", {"start": v(145.63, 69.75) * mm, "end": v(145.63, 81.75) * mm});
            skPoint(sketch, "E140.orphan", {"position": v(145.63, 40.75) * mm});
            skPoint(sketch, "E141.orphan", {"position": v(145.63, 110.75) * mm});
            skLineSegment(sketch, "E142", {"start": v(145.63, 69.75) * mm, "end": v(174.63, 69.75) * mm});
            skPoint(sketch, "E143", {"position": v(-204.37, 69.75) * mm});
            skLineSegment(sketch, "E144.0", {"start": v(145.63, -309.25) * mm, "end": v(145.63, -379.25) * mm});
            skLineSegment(sketch, "E145", {"start": v(145.63, -338.25) * mm, "end": v(174.63, -338.25) * mm});
            skPoint(sketch, "E146", {"position": v(-204.37, -338.25) * mm});
            skPoint(sketch, "E147", {"position": v(-198.37, 69.75) * mm});
            skPoint(sketch, "E148", {"position": v(-210.37, 69.75) * mm});
            skLineSegment(sketch, "E149.bottom", {"start": v(-198.37, 115.75) * mm, "end": v(-210.37, 115.75) * mm});
            skLineSegment(sketch, "E149.top", {"start": v(-198.37, -384.25) * mm, "end": v(-210.37, -384.25) * mm});
            skLineSegment(sketch, "E149.left", {"start": v(-198.37, 115.75) * mm, "end": v(-198.37, 81.75) * mm});
            skLineSegment(sketch, "E149.right", {"start": v(-210.37, 115.75) * mm, "end": v(-210.37, 81.75) * mm});
            skLineSegment(sketch, "E150.trimOffspring", {"start": v(-198.37, -350.25) * mm, "end": v(-198.37, -384.25) * mm});
            skLineSegment(sketch, "E151.trimOffspring", {"start": v(-210.37, -350.25) * mm, "end": v(-210.37, -384.25) * mm});
            skLineSegment(sketch, "E152.trimOffspring", {"start": v(-198.37, -338.25) * mm, "end": v(145.63, -338.25) * mm});
            skLineSegment(sketch, "E153.trimOffspring", {"start": v(-198.37, 69.75) * mm, "end": v(-198.37, -338.25) * mm});
            skLineSegment(sketch, "E154.trimOffspring", {"start": v(-210.37, 69.75) * mm, "end": v(-554.37, 69.75) * mm});
            skLineSegment(sketch, "E155.trimOffspring", {"start": v(-210.37, 81.75) * mm, "end": v(-554.37, 81.75) * mm});
            skLineSegment(sketch, "E156.trimOffspring", {"start": v(-210.37, 69.75) * mm, "end": v(-210.37, -338.25) * mm});
            skLineSegment(sketch, "E157.trimOffspring", {"start": v(-198.37, -350.25) * mm, "end": v(186.63, -350.25) * mm});
            skLineSegment(sketch, "E158", {"start": v(145.63, 81.75) * mm, "end": v(186.63, 81.75) * mm, "construction": true});
            skSolve(sketch);
        }
        {
            var Q0;
            {var subQ1=sQuery(id+"F27.wireOp",EDGE,"E129");Q0=makeQuery(id+"F27.imprint","IMPRINT",FACE,{"disambiguationData":[TD([[makeQuery(id+"F27.imprint","IMPRINT",EDGE,{"derivedFrom":subQ1}),1.0]])]});}
            var Q1;
            {var subQ0=sQuery(id+"F27.wireOp",EDGE,"E132");Q1=makeQuery(id+"F27.imprint","IMPRINT",FACE,{"disambiguationData":[TD([[makeQuery(id+"F27.imprint","IMPRINT",EDGE,{"derivedFrom":subQ0}),-1.0]])]});}
            var Q2;
            {var subQ0=sQuery(id+"F27.wireOp",EDGE,"E130");var subQ1=makeQuery(id+"F4.boolean.opBoolean","COPY",EDGE,{"derivedFrom":makeQuery(id+"F4.opExtrude","CAP_EDGE",EDGE,{"disambiguationData":[OSD([sQuery(id+"F3.wireOp",EDGE,"E30")])],"isStart":true})});var subQ2=makeQuery(id+"F27.imprint","INTERSECT",VERTEX,{"derivedFrom":[subQ1,subQ0]});Q2=makeQuery(id+"F27.imprint","IMPRINT",FACE,{"disambiguationData":[TD([[makeQuery(id+"F27.imprint","IMPRINT",EDGE,{"disambiguationData":[TD([[subQ2,-1.0]])],"derivedFrom":subQ0}),1.0]])]});}
            extrude(context, id + "F28", {"entities" : qUnion([Q0, Q1, Q2]), "operationType" : NewBodyOperationType.REMOVE, "oppositeDirection" : true, "depth" : 6 * mm});
        }
        {
            var Q0;
            {var subQ0=sQuery(id+"F0.wireOp",EDGE,"E0.left");var subQ1=sQuery(id+"F0.wireOp",EDGE,"E0.right");var subQ2=sQuery(id+"F0.wireOp",EDGE,"E0.top");var subQ3=sQuery(id+"F0.wireOp",EDGE,"E0.bottom");Q0=makeQuery(id+"F28.boolean.opBoolean","SPLIT",FACE,{"disambiguationData":[TD([makeQuery(id+"F1.opExtrude","SWEPT_FACE",FACE,{"disambiguationData":[OSD([subQ3])]})])],"derivedFrom":makeQuery(id+"F1.opExtrude","CAP_FACE",FACE,{"disambiguationData":[OSD([subQ3,subQ2,subQ0,subQ1])],"isStart":true})});}
            cPlane(context, id + "F29", {"entities" : qUnion([Q0]), "cplaneType" : CPlaneType.OFFSET, "offset" : 25 * mm, "width" : 150 * mm, "height" : 150 * mm});
        }
        {
            var Q0;
            Q0=qCreatedBy(id+"F29.planeOp",FACE);
            var sketch = newSketch(context, id + "F30", { "sketchPlane" : qUnion([Q0])});
            skLineSegment(sketch, "E159.bottom", {"start": v(-223.26, 121.47) * mm, "end": v(-211.4, 121.47) * mm});
            skLineSegment(sketch, "E159.top", {"start": v(-223.26, -378.33) * mm, "end": v(-211.4, -378.33) * mm});
            skLineSegment(sketch, "E159.left", {"start": v(-223.26, 121.47) * mm, "end": v(-223.26, -378.33) * mm});
            skLineSegment(sketch, "E159.right", {"start": v(-211.4, 121.47) * mm, "end": v(-211.4, -378.33) * mm});
            skLineSegment(sketch, "E160.bottom", {"start": v(-634.57, 195.64) * mm, "end": v(-249.57, 195.64) * mm});
            skLineSegment(sketch, "E160.top", {"start": v(-634.57, 183.79) * mm, "end": v(-249.57, 183.79) * mm});
            skLineSegment(sketch, "E160.left", {"start": v(-634.57, 195.64) * mm, "end": v(-634.57, 183.79) * mm});
            skLineSegment(sketch, "E160.right", {"start": v(147.43, 195.64) * mm, "end": v(147.43, 183.79) * mm});
            skPoint(sketch, "E161", {"position": v(-237.57, 195.64) * mm});
            skLineSegment(sketch, "E162.left", {"start": v(-237.57, 195.64) * mm, "end": v(-237.57, 183.79) * mm});
            skLineSegment(sketch, "E162.right", {"start": v(-249.57, 195.64) * mm, "end": v(-249.57, 183.79) * mm});
            skPoint(sketch, "E163", {"position": v(-211.4, 87.57) * mm});
            skPoint(sketch, "E164", {"position": v(-211.4, -344.43) * mm});
            skLineSegment(sketch, "E165.bottom", {"start": v(-211.4, 87.57) * mm, "end": v(-223.26, 87.57) * mm});
            skLineSegment(sketch, "E165.top", {"start": v(-211.4, 75.57) * mm, "end": v(-223.26, 75.57) * mm});
            skLineSegment(sketch, "E165.left", {"start": v(-211.4, 87.57) * mm, "end": v(-211.4, 75.57) * mm});
            skLineSegment(sketch, "E165.right", {"start": v(-223.26, 87.57) * mm, "end": v(-223.26, 75.57) * mm});
            skLineSegment(sketch, "E166.bottom", {"start": v(-211.4, -344.43) * mm, "end": v(-223.26, -344.43) * mm});
            skLineSegment(sketch, "E166.top", {"start": v(-211.4, -332.43) * mm, "end": v(-223.26, -332.43) * mm});
            skLineSegment(sketch, "E166.left", {"start": v(-211.4, -344.43) * mm, "end": v(-211.4, -332.43) * mm});
            skLineSegment(sketch, "E166.right", {"start": v(-223.26, -344.43) * mm, "end": v(-223.26, -332.43) * mm});
            skLineSegment(sketch, "E167.bottom", {"start": v(238.55, 97.1) * mm, "end": v(250.4, 97.1) * mm});
            skLineSegment(sketch, "E167.top", {"start": v(238.55, -310.9) * mm, "end": v(250.4, -310.9) * mm});
            skLineSegment(sketch, "E167.left", {"start": v(238.55, 97.1) * mm, "end": v(238.55, -310.9) * mm});
            skLineSegment(sketch, "E167.right", {"start": v(250.4, 97.1) * mm, "end": v(250.4, -310.9) * mm});
            skLineSegment(sketch, "E168.0", {"start": v(145.63, 81.75) * mm, "end": v(-198.37, 81.75) * mm});
            skLineSegment(sketch, "E169.trimOffspring", {"start": v(-237.57, 195.64) * mm, "end": v(147.43, 195.64) * mm});
            skLineSegment(sketch, "E170.trimOffspring", {"start": v(-237.57, 183.79) * mm, "end": v(147.43, 183.79) * mm});
            skLineSegment(sketch, "E171", {"start": v(-249.57, 195.64) * mm, "end": v(-237.57, 195.64) * mm});
            skLineSegment(sketch, "E172", {"start": v(-237.57, 183.79) * mm, "end": v(-249.57, 183.79) * mm});
            skSolve(sketch);
        }
        {
            var Q0;
            {var subQ0=sQuery(id+"F30.wireOp",EDGE,"E160.left");Q0=makeQuery(id+"F30.imprint","IMPRINT",FACE,{"disambiguationData":[TD([[makeQuery(id+"F30.imprint","IMPRINT",EDGE,{"derivedFrom":subQ0}),1.0]])]});}
            var Q1;
            {var subQ0=sQuery(id+"F30.wireOp",EDGE,"E160.right");Q1=makeQuery(id+"F30.imprint","IMPRINT",FACE,{"disambiguationData":[TD([[makeQuery(id+"F30.imprint","IMPRINT",EDGE,{"derivedFrom":subQ0}),-1.0]])]});}
            var Q2;
            {var subQ0=sQuery(id+"F30.wireOp",EDGE,"E159.bottom");Q2=makeQuery(id+"F30.imprint","IMPRINT",FACE,{"disambiguationData":[TD([[makeQuery(id+"F30.imprint","IMPRINT",EDGE,{"derivedFrom":subQ0}),-1.0]])]});}
            var Q3;
            {var subQ0=sQuery(id+"F30.wireOp",EDGE,"E165.top");Q3=makeQuery(id+"F30.imprint","IMPRINT",FACE,{"disambiguationData":[TD([[makeQuery(id+"F30.imprint","IMPRINT",EDGE,{"derivedFrom":subQ0}),1.0]])]});}
            var Q4;
            {var subQ0=sQuery(id+"F30.wireOp",EDGE,"E159.top");Q4=makeQuery(id+"F30.imprint","IMPRINT",FACE,{"disambiguationData":[TD([[makeQuery(id+"F30.imprint","IMPRINT",EDGE,{"derivedFrom":subQ0}),1.0]])]});}
            var Q5;
            Q5=makeQuery(id+"F30.imprint","IMPRINT",FACE,{"disambiguationData":[TD([[makeQuery(id+"F30.imprint","IMPRINT",EDGE,{"derivedFrom":sQuery(id+"F30.wireOp",EDGE,"E167.bottom")}),-1.0]])]});
            extrude(context, id + "F31", {"entities" : qUnion([Q0, Q1, Q2, Q3, Q4, Q5]), "depth" : 12 * mm});
        }
        {
            var Q0;
            Q0=makeQuery(id+"F30.imprint","IMPRINT",FACE,{"disambiguationData":[TD([[makeQuery(id+"F30.imprint","IMPRINT",EDGE,{"derivedFrom":sQuery(id+"F30.wireOp",EDGE,"E162.bottom")}),1.0]])]});
            var Q1;
            Q1=makeQuery(id+"F30.imprint","IMPRINT",FACE,{"disambiguationData":[TD([[makeQuery(id+"F30.imprint","IMPRINT",EDGE,{"derivedFrom":sQuery(id+"F30.wireOp",EDGE,"E165.bottom")}),1.0]])]});
            var Q2;
            Q2=makeQuery(id+"F30.imprint","IMPRINT",FACE,{"disambiguationData":[TD([[makeQuery(id+"F30.imprint","IMPRINT",EDGE,{"derivedFrom":sQuery(id+"F30.wireOp",EDGE,"E166.bottom")}),-1.0]])]});
            extrude(context, id + "F32", {"entities" : qUnion([Q0, Q1, Q2]), "operationType" : NewBodyOperationType.ADD, "depth" : 6 * mm});
        }
        {
            var Q0;
            Q0=makeQuery(id+"F30.imprint","IMPRINT",FACE,{"disambiguationData":[TD([[makeQuery(id+"F30.imprint","IMPRINT",EDGE,{"derivedFrom":sQuery(id+"F30.wireOp",EDGE,"E162.left")}),-1.0]])]});
            extrude(context, id + "F33", {"entities" : qUnion([Q0]), "operationType" : NewBodyOperationType.ADD, "depth" : 6 * mm});
        }
        {
            var Q0;
            Q0=makeQuery(id+"F25.opExtrude","CAP_FACE",FACE,{"disambiguationData":[OSD([sQuery(id+"F8.wireOp",EDGE,"E43.bottom"),sQuery(id+"F8.wireOp",EDGE,"E43.top"),sQuery(id+"F8.wireOp",EDGE,"E43.right"),sQuery(id+"F8.wireOp",EDGE,"E45.top"),sQuery(id+"F8.wireOp",EDGE,"E45.left"),sQuery(id+"F8.wireOp",EDGE,"E45.right"),sQuery(id+"F8.wireOp",EDGE,"E48"),sQuery(id+"F8.wireOp",EDGE,"E49")])],"isStart":false});
            var Q1;
            {var subQ0=sQuery(id+"F6.wireOp",EDGE,"E31.0");var subQ1=sQuery(id+"F6.wireOp",EDGE,"E34.0");Q1=makeQuery(id+"F24.opPattern","COPY",FACE,{"derivedFrom":makeQuery(id+"F9.boolean.opBoolean","SPLIT",FACE,{"disambiguationData":[TD([makeQuery(id+"F9.opExtrude","SWEPT_FACE",FACE,{"disambiguationData":[OSD([sQuery(id+"F8.wireOp",EDGE,"E43.bottom")])]})])],"derivedFrom":makeQuery(id+"F7.opExtrude","CAP_FACE",FACE,{"disambiguationData":[OSD([subQ0,sQuery(id+"F6.wireOp",EDGE,"E32.0"),sQuery(id+"F6.wireOp",EDGE,"E33.0"),subQ1])],"isStart":true})}),"instanceName":"1"});}
            extrude(context, id + "F34", {"entities" : qUnion([Q0]), "operationType" : NewBodyOperationType.ADD, "endBound" : BoundingType.UP_TO_SURFACE, "endBoundEntityFace" : qUnion([Q1]), "depth" : 6 * mm});
        }
        {
            var Q0;
            {var subQ0=sQuery(id+"F8.wireOp",EDGE,"E49");var subQ1=sQuery(id+"F8.wireOp",EDGE,"E48");var subQ2=sQuery(id+"F8.wireOp",EDGE,"E45.right");var subQ3=sQuery(id+"F8.wireOp",EDGE,"E45.left");var subQ4=sQuery(id+"F8.wireOp",EDGE,"E43.top");var subQ5=sQuery(id+"F8.wireOp",EDGE,"E43.bottom");var subQ6=sQuery(id+"F6.wireOp",EDGE,"E31.0");var subQ8=sQuery(id+"F6.wireOp",EDGE,"E34.0");var subQ10=sQuery(id+"F6.wireOp",EDGE,"E33.0");var subQ11=sQuery(id+"F6.wireOp",EDGE,"E32.0");var subQ12=makeQuery(id+"F7.opExtrude","CAP_FACE",FACE,{"disambiguationData":[OSD([subQ6,subQ11,subQ10,subQ8])],"isStart":true});Q0=makeQuery(id+"F34.boolean.opBoolean","MERGE",FACE,{"derivedFrom":[makeQuery(id+"F24.opPattern","COPY",FACE,{"derivedFrom":makeQuery(id+"F9.boolean.opBoolean","SPLIT",FACE,{"disambiguationData":[TD([makeQuery(id+"F7.opExtrude","SWEPT_FACE",FACE,{"disambiguationData":[OSD([subQ11])]})])],"derivedFrom":subQ12}),"instanceName":"1"}),makeQuery(id+"F24.opPattern","COPY",FACE,{"derivedFrom":makeQuery(id+"F9.boolean.opBoolean","SPLIT",FACE,{"disambiguationData":[TD([makeQuery(id+"F9.opExtrude","SWEPT_FACE",FACE,{"disambiguationData":[OSD([subQ5])]})])],"derivedFrom":subQ12}),"instanceName":"1"}),makeQuery(id+"F34.opExtrude","CAP_FACE",FACE,{"disambiguationData":[OSD([subQ5,subQ4,sQuery(id+"F8.wireOp",EDGE,"E43.right"),sQuery(id+"F8.wireOp",EDGE,"E45.top"),subQ3,subQ2,subQ1,subQ0])],"isStart":false})]});}
            extrude(context, id + "F35", {"entities" : qUnion([Q0]), "operationType" : NewBodyOperationType.REMOVE, "oppositeDirection" : true, "depth" : 8.8 * mm});
        }
        {
            var Q0;
            Q0=makeQuery(id+"F35.boolean.opBoolean","COPY",FACE,{"derivedFrom":makeQuery(id+"F35.opExtrude","CAP_FACE",FACE,{"disambiguationData":[OSD([sQuery(id+"F6.wireOp",EDGE,"E31.0"),sQuery(id+"F6.wireOp",EDGE,"E32.0"),sQuery(id+"F6.wireOp",EDGE,"E33.0"),sQuery(id+"F6.wireOp",EDGE,"E34.0"),sQuery(id+"F8.wireOp",EDGE,"E43.bottom"),sQuery(id+"F8.wireOp",EDGE,"E43.top"),sQuery(id+"F8.wireOp",EDGE,"E43.right"),sQuery(id+"F8.wireOp",EDGE,"E45.top"),sQuery(id+"F8.wireOp",EDGE,"E45.left"),sQuery(id+"F8.wireOp",EDGE,"E45.right"),sQuery(id+"F8.wireOp",EDGE,"E48"),sQuery(id+"F8.wireOp",EDGE,"E49")])],"isStart":false})});
            var sketch = newSketch(context, id + "F36", { "sketchPlane" : qUnion([Q0])});
            skLineSegment(sketch, "E173.0", {"start": v(-539.37, 95.75) * mm, "end": v(-539.37, 195.75) * mm});
            skLineSegment(sketch, "E173.1", {"start": v(-639.37, 95.75) * mm, "end": v(-539.37, 95.75) * mm});
            skLineSegment(sketch, "E173.2", {"start": v(-639.37, 195.75) * mm, "end": v(-639.37, 95.75) * mm});
            skLineSegment(sketch, "E173.3", {"start": v(-539.37, 195.75) * mm, "end": v(-639.37, 195.75) * mm});
            skSolve(sketch);
        }
        {
            var Q0;
            Q0=makeQuery(id+"F36.imprint","IMPRINT",FACE,{"disambiguationData":[TD([[makeQuery(id+"F36.imprint","IMPRINT",EDGE,{"derivedFrom":sQuery(id+"F36.wireOp",EDGE,"E173.0")}),1.0]])]});
            extrude(context, id + "F37", {"entities" : qUnion([Q0]), "operationType" : NewBodyOperationType.ADD, "oppositeDirection" : true, "depth" : 6 * mm});
        }
        {
            var Q0;
            {var subQ6=sQuery(id+"F27.wireOp",EDGE,"E133.0");Q0=makeQuery(id+"F27.imprint","IMPRINT",FACE,{"disambiguationData":[TD([[makeQuery(id+"F27.imprint","IMPRINT",EDGE,{"derivedFrom":subQ6}),1.0]])]});}
            var sketch = newSketch(context, id + "F38", { "sketchPlane" : qUnion([Q0])});
            skLineSegment(sketch, "E174.0", {"start": v(-198.37, -350.25) * mm, "end": v(186.63, -350.25) * mm});
            skPoint(sketch, "E175.0", {"position": v(-595.37, -350.25) * mm});
            skLineSegment(sketch, "E176.0", {"start": v(-554.37, -350.25) * mm, "end": v(-595.37, -350.25) * mm});
            skLineSegment(sketch, "E177.0", {"start": v(-595.37, -350.25) * mm, "end": v(-595.37, -309.25) * mm});
            skLineSegment(sketch, "E178.0", {"start": v(-595.37, 81.75) * mm, "end": v(-595.37, 40.75) * mm});
            skLineSegment(sketch, "E179.0", {"start": v(-554.37, 81.75) * mm, "end": v(-595.37, 81.75) * mm});
            skLineSegment(sketch, "E180.0", {"start": v(186.63, -350.25) * mm, "end": v(186.63, 81.75) * mm});
            skPoint(sketch, "E181.0", {"position": v(166.13, 81.75) * mm});
            skLineSegment(sketch, "E182.0", {"start": v(145.63, 81.75) * mm, "end": v(186.63, 81.75) * mm});
            skLineSegment(sketch, "E183.bottom", {"start": v(-598.28, -647.52) * mm, "end": v(183.72, -647.52) * mm});
            skLineSegment(sketch, "E183.top", {"start": v(-598.28, -679.52) * mm, "end": v(183.72, -679.52) * mm});
            skLineSegment(sketch, "E183.left", {"start": v(-598.28, -647.52) * mm, "end": v(-598.28, -657.47) * mm});
            skLineSegment(sketch, "E183.right", {"start": v(183.72, -647.52) * mm, "end": v(183.72, -657.47) * mm});
            skLineSegment(sketch, "E184.0", {"start": v(-583.37, 69.75) * mm, "end": v(-554.37, 69.75) * mm});
            skLineSegment(sketch, "E185.0", {"start": v(-583.37, 69.75) * mm, "end": v(-583.37, 40.75) * mm});
            skPoint(sketch, "E186", {"position": v(-572.23, -647.52) * mm});
            skPoint(sketch, "E187", {"position": v(-598.28, -657.47) * mm});
            skPoint(sketch, "E188", {"position": v(-598.28, -669.57) * mm});
            skLineSegment(sketch, "E189.trimOffspring", {"start": v(-598.28, -669.57) * mm, "end": v(-598.28, -679.52) * mm});
            skLineSegment(sketch, "E190.bottom", {"start": v(-598.28, -657.47) * mm, "end": v(-572.23, -657.47) * mm});
            skLineSegment(sketch, "E190.top", {"start": v(-598.28, -669.57) * mm, "end": v(-572.23, -669.57) * mm});
            skLineSegment(sketch, "E190.right", {"start": v(-572.23, -657.47) * mm, "end": v(-572.23, -669.57) * mm});
            skLineSegment(sketch, "E191", {"start": v(-207.28, -647.52) * mm, "end": v(-207.28, -679.52) * mm, "construction": true});
            skLineSegment(sketch, "E192.MirrorCS", {"start": v(183.72, -657.47) * mm, "end": v(157.67, -657.47) * mm});
            skLineSegment(sketch, "E193.MirrorCS", {"start": v(157.67, -657.47) * mm, "end": v(157.67, -669.57) * mm});
            skLineSegment(sketch, "E194.MirrorCS", {"start": v(183.72, -669.57) * mm, "end": v(157.67, -669.57) * mm});
            skLineSegment(sketch, "E195.trimOffspring", {"start": v(183.72, -669.57) * mm, "end": v(183.72, -679.52) * mm});
            skLineSegment(sketch, "E196.bottom", {"start": v(479.6, 83.02) * mm, "end": v(469.64, 83.02) * mm});
            skLineSegment(sketch, "E196.top", {"start": v(479.6, -348.98) * mm, "end": v(469.64, -348.98) * mm});
            skLineSegment(sketch, "E196.left", {"start": v(479.6, 83.02) * mm, "end": v(479.6, -348.98) * mm});
            skLineSegment(sketch, "E196.right", {"start": v(447.6, 83.02) * mm, "end": v(447.6, -348.98) * mm});
            skPoint(sketch, "E197", {"position": v(457.54, 83.02) * mm});
            skPoint(sketch, "E198", {"position": v(469.64, 83.02) * mm});
            skLineSegment(sketch, "E199.trimOffspring", {"start": v(457.54, 83.02) * mm, "end": v(447.6, 83.02) * mm});
            skPoint(sketch, "E200", {"position": v(479.6, 56.97) * mm});
            skLineSegment(sketch, "E201.top", {"start": v(457.54, 56.97) * mm, "end": v(469.64, 56.97) * mm});
            skLineSegment(sketch, "E201.left", {"start": v(457.54, 83.02) * mm, "end": v(457.54, 56.97) * mm});
            skLineSegment(sketch, "E201.right", {"start": v(469.64, 83.02) * mm, "end": v(469.64, 56.97) * mm});
            skLineSegment(sketch, "E202", {"start": v(479.6, -132.98) * mm, "end": v(458.37, -132.98) * mm, "construction": true});
            skLineSegment(sketch, "E203.MirrorCS", {"start": v(457.54, -348.98) * mm, "end": v(457.54, -322.93) * mm});
            skLineSegment(sketch, "E204.MirrorCS", {"start": v(469.64, -348.98) * mm, "end": v(469.64, -322.93) * mm});
            skLineSegment(sketch, "E205.MirrorCS", {"start": v(457.54, -322.93) * mm, "end": v(469.64, -322.93) * mm});
            skLineSegment(sketch, "E206.trimOffspring", {"start": v(457.54, -348.98) * mm, "end": v(447.6, -348.98) * mm});
            skLineSegment(sketch, "E207.left", {"start": v(447.6, 43.7) * mm, "end": v(447.6, -206.3) * mm});
            skSolve(sketch);
        }
        {
            var Q0;
            Q0=makeQuery(id+"F38.imprint","IMPRINT",FACE,{"disambiguationData":[TD([[makeQuery(id+"F38.imprint","IMPRINT",EDGE,{"derivedFrom":sQuery(id+"F38.wireOp",EDGE,"E183.bottom")}),-1.0]])]});
            var Q1;
            Q1=makeQuery(id+"F38.imprint","IMPRINT",FACE,{"disambiguationData":[TD([[makeQuery(id+"F38.imprint","IMPRINT",EDGE,{"derivedFrom":sQuery(id+"F38.wireOp",EDGE,"E196.bottom")}),1.0]])]});
            var Q2;
            Q2=makeQuery(id+"F38.imprint","IMPRINT",FACE,{"disambiguationData":[TD([[makeQuery(id+"F38.imprint","IMPRINT",EDGE,{"derivedFrom":sQuery(id+"F38.wireOp",EDGE,"E207.bottom")}),1.0]])]});
            extrude(context, id + "F39", {"entities" : qUnion([Q0, Q1, Q2]), "depth" : 12 * mm});
        }
        {
            var Q0;
            Q0=makeQuery(id+"F1.opExtrude","SWEPT_EDGE",EDGE,{"disambiguationData":[OSD([sQuery(id+"F0.wireOp",EDGE,"E0.bottom"),sQuery(id+"F0.wireOp",EDGE,"E0.left")])]});
            var Q1;
            Q1=makeQuery(id+"F1.opExtrude","SWEPT_EDGE",EDGE,{"disambiguationData":[OSD([sQuery(id+"F0.wireOp",EDGE,"E0.top"),sQuery(id+"F0.wireOp",EDGE,"E0.left")])]});
            var Q2;
            Q2=makeQuery(id+"F1.opExtrude","SWEPT_EDGE",EDGE,{"disambiguationData":[OSD([sQuery(id+"F0.wireOp",EDGE,"E0.top"),sQuery(id+"F0.wireOp",EDGE,"E0.right")])]});
            var Q3;
            Q3=makeQuery(id+"F1.opExtrude","SWEPT_EDGE",EDGE,{"disambiguationData":[OSD([sQuery(id+"F0.wireOp",EDGE,"E0.bottom"),sQuery(id+"F0.wireOp",EDGE,"E0.right")])]});
            fillet(context, id + "F40", {"entities" : qUnion([Q0, Q1, Q2, Q3]), "radius" : 45 * mm, "tangentPropagation" : true, "allowEdgeOverflow" : false});
        }
        {
            var Q0;
            Q0=makeQuery(id+"F1.opExtrude","CAP_FACE",FACE,{"disambiguationData":[OSD([sQuery(id+"F0.wireOp",EDGE,"E0.bottom"),sQuery(id+"F0.wireOp",EDGE,"E0.top"),sQuery(id+"F0.wireOp",EDGE,"E0.left"),sQuery(id+"F0.wireOp",EDGE,"E0.right")])],"isStart":false});
            var sketch = newSketch(context, id + "F41", { "sketchPlane" : qUnion([Q0])});
            skArc(sketch, "E208.0.0", {"start": v(250.63, 429.25) * mm, "mid": v(278.91, 417.53) * mm, "end": v(290.63, 389.25) * mm});
            skLineSegment(sketch, "E208.0.1", {"start": v(250.63, 429.25) * mm, "end": v(-659.37, 429.25) * mm});
            skArc(sketch, "E208.0.2", {"start": v(-699.37, 389.25) * mm, "mid": v(-687.65, 417.53) * mm, "end": v(-659.37, 429.25) * mm});
            skLineSegment(sketch, "E208.0.3", {"start": v(-699.37, 389.25) * mm, "end": v(-699.37, -120.75) * mm});
            skArc(sketch, "E208.0.4", {"start": v(-659.37, -160.75) * mm, "mid": v(-687.65, -149.03) * mm, "end": v(-699.37, -120.75) * mm});
            skLineSegment(sketch, "E208.0.5", {"start": v(-659.37, -160.75) * mm, "end": v(250.63, -160.75) * mm});
            skArc(sketch, "E208.0.6", {"start": v(290.63, -120.75) * mm, "mid": v(278.91, -149.03) * mm, "end": v(250.63, -160.75) * mm});
            skLineSegment(sketch, "E208.0.7", {"start": v(290.63, -120.75) * mm, "end": v(290.63, 389.25) * mm});
            skLineSegment(sketch, "E209.bottom", {"start": v(250.63, 389.25) * mm, "end": v(262.73, 389.25) * mm});
            skLineSegment(sketch, "E209.top", {"start": v(250.63, 139.25) * mm, "end": v(262.73, 139.25) * mm});
            skLineSegment(sketch, "E209.left", {"start": v(250.63, 377.15) * mm, "end": v(250.63, 139.25) * mm});
            skLineSegment(sketch, "E209.right", {"start": v(262.73, 389.25) * mm, "end": v(262.73, 369.25) * mm});
            skPoint(sketch, "E210", {"position": v(250.63, 377.15) * mm});
            skLineSegment(sketch, "E211.bottom", {"start": v(250.63, 389.25) * mm, "end": v(250.63, 389.25) * mm});
            skLineSegment(sketch, "E211.top", {"start": v(250.63, 377.15) * mm, "end": v(250.63, 377.15) * mm});
            skLineSegment(sketch, "E212.bottom", {"start": v(191.33, 389.25) * mm, "end": v(171.33, 389.25) * mm});
            skLineSegment(sketch, "E212.top", {"start": v(250.63, 377.15) * mm, "end": v(12.73, 377.15) * mm});
            skLineSegment(sketch, "E212.right", {"start": v(12.73, 389.25) * mm, "end": v(12.73, 377.15) * mm});
            skPoint(sketch, "E213", {"position": v(262.73, 312.58) * mm});
            skPoint(sketch, "E214", {"position": v(262.73, 292.58) * mm});
            skPoint(sketch, "E215", {"position": v(262.73, 235.92) * mm});
            skPoint(sketch, "E216", {"position": v(262.73, 215.92) * mm});
            skPoint(sketch, "E217", {"position": v(262.73, 159.25) * mm});
            skLineSegment(sketch, "E218.trimOffspring", {"start": v(262.73, 159.25) * mm, "end": v(262.73, 139.25) * mm});
            skLineSegment(sketch, "E219.trimOffspring", {"start": v(262.73, 235.92) * mm, "end": v(262.73, 215.92) * mm});
            skLineSegment(sketch, "E220.trimOffspring", {"start": v(262.73, 312.58) * mm, "end": v(262.73, 292.58) * mm});
            skLineSegment(sketch, "E221", {"start": v(250.63, 389.25) * mm, "end": v(250.63, 377.15) * mm});
            skLineSegment(sketch, "E222", {"start": v(262.73, 369.25) * mm, "end": v(250.63, 369.25) * mm});
            skLineSegment(sketch, "E223", {"start": v(262.73, 369.25) * mm, "end": v(262.73, 312.58) * mm});
            skLineSegment(sketch, "E224", {"start": v(262.73, 292.58) * mm, "end": v(262.73, 235.92) * mm});
            skLineSegment(sketch, "E225", {"start": v(262.73, 215.92) * mm, "end": v(262.73, 159.25) * mm});
            skLineSegment(sketch, "E226", {"start": v(262.73, 159.25) * mm, "end": v(250.63, 159.25) * mm});
            skLineSegment(sketch, "E227", {"start": v(262.73, 215.92) * mm, "end": v(250.63, 215.92) * mm});
            skLineSegment(sketch, "E228", {"start": v(262.73, 235.92) * mm, "end": v(250.63, 235.92) * mm});
            skLineSegment(sketch, "E229", {"start": v(262.73, 292.58) * mm, "end": v(250.63, 292.58) * mm});
            skLineSegment(sketch, "E230", {"start": v(262.73, 312.58) * mm, "end": v(250.63, 312.58) * mm});
            skPoint(sketch, "E231", {"position": v(191.33, 389.25) * mm});
            skPoint(sketch, "E232", {"position": v(171.33, 389.25) * mm});
            skPoint(sketch, "E233", {"position": v(112.03, 389.25) * mm});
            skPoint(sketch, "E234", {"position": v(92.03, 389.25) * mm});
            skPoint(sketch, "E235", {"position": v(32.73, 389.25) * mm});
            skLineSegment(sketch, "E236.trimOffspring", {"start": v(32.73, 389.25) * mm, "end": v(12.73, 389.25) * mm});
            skLineSegment(sketch, "E237.trimOffspring", {"start": v(112.03, 389.25) * mm, "end": v(92.03, 389.25) * mm});
            skLineSegment(sketch, "E238", {"start": v(32.73, 389.25) * mm, "end": v(92.03, 389.25) * mm});
            skLineSegment(sketch, "E239", {"start": v(112.03, 389.25) * mm, "end": v(171.33, 389.25) * mm});
            skLineSegment(sketch, "E240", {"start": v(191.33, 389.25) * mm, "end": v(250.63, 389.25) * mm});
            skLineSegment(sketch, "E241", {"start": v(32.73, 389.25) * mm, "end": v(32.73, 377.15) * mm});
            skLineSegment(sketch, "E242", {"start": v(112.03, 389.25) * mm, "end": v(112.03, 377.15) * mm});
            skLineSegment(sketch, "E243", {"start": v(92.03, 389.25) * mm, "end": v(92.03, 377.15) * mm});
            skLineSegment(sketch, "E244", {"start": v(171.33, 389.25) * mm, "end": v(171.33, 377.15) * mm});
            skLineSegment(sketch, "E245", {"start": v(191.33, 389.25) * mm, "end": v(191.33, 377.15) * mm});
            skSolve(sketch);
        }
        {
            var Q0;
            {var subQ0=sQuery(id+"F41.wireOp",EDGE,"E212.right");Q0=makeQuery(id+"F41.imprint","IMPRINT",FACE,{"disambiguationData":[TD([[makeQuery(id+"F41.imprint","IMPRINT",EDGE,{"derivedFrom":subQ0}),1.0]])]});}
            var Q1;
            Q1=makeQuery(id+"F41.imprint","IMPRINT",FACE,{"disambiguationData":[TD([[makeQuery(id+"F41.imprint","IMPRINT",EDGE,{"derivedFrom":sQuery(id+"F41.wireOp",EDGE,"E237.trimOffspring")}),1.0]])]});
            var Q2;
            Q2=makeQuery(id+"F41.imprint","IMPRINT",FACE,{"disambiguationData":[TD([[makeQuery(id+"F41.imprint","IMPRINT",EDGE,{"derivedFrom":sQuery(id+"F41.wireOp",EDGE,"E212.bottom")}),1.0]])]});
            var Q3;
            Q3=makeQuery(id+"F41.imprint","IMPRINT",FACE,{"disambiguationData":[TD([[makeQuery(id+"F41.imprint","IMPRINT",EDGE,{"derivedFrom":sQuery(id+"F41.wireOp",EDGE,"E209.bottom")}),-1.0]])]});
            var Q4;
            Q4=makeQuery(id+"F41.imprint","IMPRINT",FACE,{"disambiguationData":[TD([[makeQuery(id+"F41.imprint","IMPRINT",EDGE,{"derivedFrom":sQuery(id+"F41.wireOp",EDGE,"E220.trimOffspring")}),-1.0]])]});
            var Q5;
            Q5=makeQuery(id+"F41.imprint","IMPRINT",FACE,{"disambiguationData":[TD([[makeQuery(id+"F41.imprint","IMPRINT",EDGE,{"derivedFrom":sQuery(id+"F41.wireOp",EDGE,"E219.trimOffspring")}),-1.0]])]});
            var Q6;
            {var subQ0=sQuery(id+"F41.wireOp",EDGE,"E209.top");Q6=makeQuery(id+"F41.imprint","IMPRINT",FACE,{"disambiguationData":[TD([[makeQuery(id+"F41.imprint","IMPRINT",EDGE,{"derivedFrom":subQ0}),1.0]])]});}
            extrude(context, id + "F42", {"entities" : qUnion([Q0, Q1, Q2, Q3, Q4, Q5, Q6]), "operationType" : NewBodyOperationType.REMOVE, "oppositeDirection" : true, "depth" : 6 * mm});
        }
        {
            var Q0;
            Q0=sQuery(id+"F41.wireOp",EDGE,"E223");
            cPlane(context, id + "F43", {"entities" : qUnion([Q0]), "cplaneType" : CPlaneType.LINE_ANGLE, "offset" : 25 * mm, "angle" : 90 * degree, "width" : 150 * mm, "height" : 150 * mm});
        }
        {
            var Q0;
            Q0=qCreatedBy(id+"F43.planeOp",FACE);
            var sketch = newSketch(context, id + "F44", { "sketchPlane" : qUnion([Q0])});
            skLineSegment(sketch, "E246.0", {"start": v(389.25, 12) * mm, "end": v(369.25, 12) * mm});
            skLineSegment(sketch, "E247.0", {"start": v(369.25, 12) * mm, "end": v(312.58, 12) * mm});
            skLineSegment(sketch, "E248.0", {"start": v(312.58, 12) * mm, "end": v(292.58, 12) * mm});
            skLineSegment(sketch, "E249.0", {"start": v(292.58, 12) * mm, "end": v(235.92, 12) * mm});
            skLineSegment(sketch, "E250.0", {"start": v(235.92, 12) * mm, "end": v(215.92, 12) * mm});
            skLineSegment(sketch, "E251.0", {"start": v(215.92, 12) * mm, "end": v(159.25, 12) * mm});
            skLineSegment(sketch, "E252.0", {"start": v(159.25, 12) * mm, "end": v(139.25, 12) * mm});
            skLineSegment(sketch, "E253.0", {"start": v(159.25, 52) * mm, "end": v(139.25, 52) * mm});
            skLineSegment(sketch, "E253.2", {"start": v(235.92, 52) * mm, "end": v(215.92, 52) * mm});
            skLineSegment(sketch, "E253.3", {"start": v(387.18, 52) * mm, "end": v(369.25, 52) * mm});
            skLineSegment(sketch, "E253.5", {"start": v(312.58, 52) * mm, "end": v(292.58, 52) * mm});
            skLineSegment(sketch, "E254.bottom", {"start": v(139.25, 52) * mm, "end": v(159.25, 52) * mm});
            skLineSegment(sketch, "E254.top", {"start": v(139.25, 58) * mm, "end": v(159.25, 58) * mm});
            skLineSegment(sketch, "E254.left", {"start": v(139.25, 52) * mm, "end": v(139.25, 58) * mm});
            skLineSegment(sketch, "E254.right", {"start": v(159.25, 52) * mm, "end": v(159.25, 58) * mm});
            skLineSegment(sketch, "E255.bottom", {"start": v(215.92, 52) * mm, "end": v(235.92, 52) * mm});
            skLineSegment(sketch, "E255.top", {"start": v(215.92, 58) * mm, "end": v(235.92, 58) * mm});
            skLineSegment(sketch, "E255.left", {"start": v(215.92, 52) * mm, "end": v(215.92, 58) * mm});
            skLineSegment(sketch, "E255.right", {"start": v(235.92, 52) * mm, "end": v(235.92, 58) * mm});
            skLineSegment(sketch, "E256.top", {"start": v(387.18, 58) * mm, "end": v(369.25, 58) * mm});
            skLineSegment(sketch, "E256.left", {"start": v(387.18, 52) * mm, "end": v(387.18, 58) * mm});
            skLineSegment(sketch, "E256.right", {"start": v(369.25, 52) * mm, "end": v(369.25, 58) * mm});
            skLineSegment(sketch, "E257.top", {"start": v(312.58, 58) * mm, "end": v(292.58, 58) * mm});
            skLineSegment(sketch, "E257.left", {"start": v(312.58, 52) * mm, "end": v(312.58, 58) * mm});
            skLineSegment(sketch, "E257.right", {"start": v(292.58, 52) * mm, "end": v(292.58, 58) * mm});
            skLineSegment(sketch, "E258", {"start": v(159.25, 58) * mm, "end": v(215.92, 58) * mm});
            skLineSegment(sketch, "E259", {"start": v(235.92, 58) * mm, "end": v(292.58, 58) * mm});
            skLineSegment(sketch, "E260", {"start": v(312.58, 58) * mm, "end": v(369.25, 58) * mm});
            skLineSegment(sketch, "E261.bottom", {"start": v(387.18, 58) * mm, "end": v(139.25, 58) * mm});
            skLineSegment(sketch, "E261.top", {"start": v(375.08, 308) * mm, "end": v(139.25, 308) * mm});
            skLineSegment(sketch, "E261.left", {"start": v(387.18, 58) * mm, "end": v(387.18, 78) * mm});
            skLineSegment(sketch, "E261.right", {"start": v(139.25, 58) * mm, "end": v(139.25, 308) * mm});
            skPoint(sketch, "E262", {"position": v(387.18, 78) * mm});
            skLineSegment(sketch, "E263.bottom", {"start": v(387.18, 78) * mm, "end": v(375.08, 78) * mm});
            skLineSegment(sketch, "E263.top", {"start": v(387.18, 58) * mm, "end": v(375.08, 58) * mm});
            skLineSegment(sketch, "E263.left", {"start": v(387.18, 78) * mm, "end": v(387.18, 58) * mm});
            skLineSegment(sketch, "E263.right", {"start": v(375.08, 78) * mm, "end": v(375.08, 58) * mm});
            skPoint(sketch, "E264", {"position": v(387.18, 154.67) * mm});
            skPoint(sketch, "E265", {"position": v(387.18, 174.67) * mm});
            skPoint(sketch, "E266", {"position": v(387.18, 231.33) * mm});
            skPoint(sketch, "E267", {"position": v(387.18, 251.33) * mm});
            skLineSegment(sketch, "E268", {"start": v(387.18, 251.33) * mm, "end": v(387.18, 231.33) * mm});
            skLineSegment(sketch, "E269.bottom", {"start": v(387.18, 174.67) * mm, "end": v(375.08, 174.67) * mm});
            skLineSegment(sketch, "E269.top", {"start": v(387.18, 154.67) * mm, "end": v(375.08, 154.67) * mm});
            skLineSegment(sketch, "E269.left", {"start": v(387.18, 174.67) * mm, "end": v(387.18, 154.67) * mm});
            skLineSegment(sketch, "E269.right", {"start": v(375.08, 174.67) * mm, "end": v(375.08, 154.67) * mm});
            skLineSegment(sketch, "E270.bottom", {"start": v(387.18, 251.33) * mm, "end": v(375.08, 251.33) * mm});
            skLineSegment(sketch, "E270.top", {"start": v(387.18, 231.33) * mm, "end": v(375.08, 231.33) * mm});
            skLineSegment(sketch, "E270.right", {"start": v(375.08, 251.33) * mm, "end": v(375.08, 231.33) * mm});
            skLineSegment(sketch, "E271", {"start": v(375.08, 251.33) * mm, "end": v(375.08, 308) * mm});
            skLineSegment(sketch, "E272", {"start": v(375.08, 174.67) * mm, "end": v(375.08, 231.33) * mm});
            skLineSegment(sketch, "E273", {"start": v(375.08, 78) * mm, "end": v(375.08, 154.67) * mm});
            skPoint(sketch, "E274.orphan", {"position": v(387.18, 308) * mm});
            skSolve(sketch);
        }
        {
            var Q0;
            Q0 = qSketchRegion(id + "F44", true);
            extrude(context, id + "F45", {"entities" : qUnion([Q0]), "depth" : 12 * mm});
        }
        {
            var Q0;
            Q0=sQuery(id+"F41.wireOp",EDGE,"E239");
            cPlane(context, id + "F46", {"entities" : qUnion([Q0]), "cplaneType" : CPlaneType.LINE_ANGLE, "offset" : 25 * mm, "angle" : 0 * degree, "width" : 150 * mm, "height" : 150 * mm});
        }
        {
            var Q0;
            Q0=qCreatedBy(id+"F46.planeOp",FACE);
            var sketch = newSketch(context, id + "F47", { "sketchPlane" : qUnion([Q0])});
            skLineSegment(sketch, "E275.0.1", {"start": v(-262.73, 308) * mm, "end": v(-274.73, 308) * mm});
            skLineSegment(sketch, "E276.0.2", {"start": v(-274.73, 308) * mm, "end": v(-274.73, 251.38) * mm});
            skLineSegment(sketch, "E277.0.2", {"start": v(-274.73, 230.83) * mm, "end": v(-274.73, 175.17) * mm});
            skLineSegment(sketch, "E278.0.2", {"start": v(-274.73, 154.62) * mm, "end": v(-274.73, 78.05) * mm});
            skLineSegment(sketch, "E279.1", {"start": v(-274.68, 78.05) * mm, "end": v(-262.78, 78.05) * mm});
            skLineSegment(sketch, "E279.3", {"start": v(-262.78, 154.62) * mm, "end": v(-274.68, 154.62) * mm});
            skLineSegment(sketch, "E280", {"start": v(-262.78, 78.05) * mm, "end": v(-262.73, 78.05) * mm});
            skLineSegment(sketch, "E281", {"start": v(-274.68, 78.05) * mm, "end": v(-274.73, 78.05) * mm});
            skPoint(sketch, "E282.orphan", {"position": v(-274.73, 78) * mm});
            skLineSegment(sketch, "E283", {"start": v(-262.73, 308) * mm, "end": v(-262.68, 308) * mm});
            skLineSegment(sketch, "E284", {"start": v(-262.68, 251.38) * mm, "end": v(-262.68, 230.83) * mm});
            skLineSegment(sketch, "E285", {"start": v(-262.68, 78.05) * mm, "end": v(-262.73, 78.05) * mm});
            skPoint(sketch, "E278.0.0.end.orphan", {"position": v(-262.73, 154.67) * mm});
            skPoint(sketch, "E286.0.start.orphan", {"position": v(-274.73, 154.67) * mm});
            skLineSegment(sketch, "E287", {"start": v(-274.68, 154.62) * mm, "end": v(-274.73, 154.62) * mm});
            skLineSegment(sketch, "E288", {"start": v(-262.78, 154.62) * mm, "end": v(-262.68, 154.62) * mm});
            skLineSegment(sketch, "E289.0", {"start": v(-274.73, 175.17) * mm, "end": v(-262.73, 175.17) * mm});
            skPoint(sketch, "E290.0.end.orphan", {"position": v(-262.73, 174.67) * mm});
            skPoint(sketch, "E290.0.start.orphan", {"position": v(-274.73, 174.67) * mm});
            skLineSegment(sketch, "E291", {"start": v(-262.73, 175.17) * mm, "end": v(-262.68, 175.17) * mm});
            skLineSegment(sketch, "E292.0", {"start": v(-262.73, 230.83) * mm, "end": v(-274.73, 230.83) * mm});
            skLineSegment(sketch, "E293", {"start": v(-262.73, 230.83) * mm, "end": v(-262.68, 230.83) * mm});
            skPoint(sketch, "E277.0.1.end.orphan", {"position": v(-274.73, 231.33) * mm});
            skPoint(sketch, "E277.0.1.start.orphan", {"position": v(-262.73, 231.33) * mm});
            skLineSegment(sketch, "E294.0", {"start": v(-274.73, 251.38) * mm, "end": v(-262.73, 251.38) * mm});
            skPoint(sketch, "E275.0.3.end.orphan", {"position": v(-262.73, 251.33) * mm});
            skPoint(sketch, "E295.orphan", {"position": v(-274.73, 251.33) * mm});
            skLineSegment(sketch, "E296", {"start": v(-262.73, 251.38) * mm, "end": v(-262.68, 251.38) * mm});
            skLineSegment(sketch, "E297", {"start": v(-12.68, 78.05) * mm, "end": v(-12.68, 328.05) * mm});
            skLineSegment(sketch, "E298", {"start": v(-262.68, 308) * mm, "end": v(-12.68, 308) * mm});
            skPoint(sketch, "E299.0", {"position": v(-274.73, 58) * mm});
            skLineSegment(sketch, "E300", {"start": v(-274.73, 58) * mm, "end": v(-12.68, 58) * mm});
            skLineSegment(sketch, "E301", {"start": v(-12.68, 58) * mm, "end": v(-12.68, 78.05) * mm});
            skLineSegment(sketch, "E302", {"start": v(-262.68, 78.05) * mm, "end": v(-262.68, 58) * mm});
            skLineSegment(sketch, "E303.trimOffspring", {"start": v(-262.68, 175.17) * mm, "end": v(-262.68, 154.62) * mm});
            skSolve(sketch);
        }
        {
            var Q0;
            Q0=makeQuery(id+"F47.imprint","IMPRINT",FACE,{"disambiguationData":[TD([[makeQuery(id+"F47.imprint","IMPRINT",EDGE,{"derivedFrom":sQuery(id+"F47.wireOp",EDGE,"E275.0.1")}),1.0]])]});
            extrude(context, id + "F48", {"entities" : qUnion([Q0]), "depth" : 12 * mm});
        }
        {
            var Q0;
            Q0=makeQuery(id+"F48.opExtrude","SWEPT_FACE",FACE,{"disambiguationData":[OSD([sQuery(id+"F47.wireOp",EDGE,"E300")])]});
            var sketch = newSketch(context, id + "F49", { "sketchPlane" : qUnion([Q0])});
            skLineSegment(sketch, "E304.0.0", {"start": v(191.33, -377.15) * mm, "end": v(191.33, -389.25) * mm});
            skLineSegment(sketch, "E304.0.1", {"start": v(191.33, -389.25) * mm, "end": v(171.33, -389.25) * mm});
            skLineSegment(sketch, "E304.0.2", {"start": v(171.33, -389.25) * mm, "end": v(171.33, -377.15) * mm});
            skLineSegment(sketch, "E304.0.3", {"start": v(171.33, -377.15) * mm, "end": v(191.33, -377.15) * mm});
            skLineSegment(sketch, "E305.0.0", {"start": v(112.03, -377.15) * mm, "end": v(112.03, -389.25) * mm});
            skLineSegment(sketch, "E305.0.1", {"start": v(112.03, -389.25) * mm, "end": v(92.03, -389.25) * mm});
            skLineSegment(sketch, "E305.0.2", {"start": v(92.03, -389.25) * mm, "end": v(92.03, -377.15) * mm});
            skLineSegment(sketch, "E305.0.3", {"start": v(92.03, -377.15) * mm, "end": v(112.03, -377.15) * mm});
            skLineSegment(sketch, "E306.0.0", {"start": v(32.73, -377.15) * mm, "end": v(32.73, -389.25) * mm});
            skLineSegment(sketch, "E306.0.1", {"start": v(32.73, -389.25) * mm, "end": v(12.73, -389.25) * mm});
            skLineSegment(sketch, "E306.0.2", {"start": v(12.73, -389.25) * mm, "end": v(12.73, -377.15) * mm});
            skLineSegment(sketch, "E306.0.3", {"start": v(12.73, -377.15) * mm, "end": v(32.73, -377.15) * mm});
            skLineSegment(sketch, "E307.MirrorCS", {"start": v(191.33, -401.35) * mm, "end": v(191.33, -389.25) * mm});
            skLineSegment(sketch, "E308.MirrorCS", {"start": v(171.33, -401.35) * mm, "end": v(191.33, -401.35) * mm});
            skLineSegment(sketch, "E309.MirrorCS", {"start": v(171.33, -389.25) * mm, "end": v(171.33, -401.35) * mm});
            skLineSegment(sketch, "E310.MirrorCS", {"start": v(112.03, -401.35) * mm, "end": v(112.03, -389.25) * mm});
            skLineSegment(sketch, "E311.MirrorCS", {"start": v(92.03, -401.35) * mm, "end": v(112.03, -401.35) * mm});
            skLineSegment(sketch, "E312.MirrorCS", {"start": v(92.03, -389.25) * mm, "end": v(92.03, -401.35) * mm});
            skLineSegment(sketch, "E313.MirrorCS", {"start": v(32.73, -401.35) * mm, "end": v(32.73, -389.25) * mm});
            skLineSegment(sketch, "E314.MirrorCS", {"start": v(12.73, -401.35) * mm, "end": v(32.73, -401.35) * mm});
            skLineSegment(sketch, "E315.MirrorCS", {"start": v(12.73, -389.25) * mm, "end": v(12.73, -401.35) * mm});
            skSolve(sketch);
        }
        {
            var Q0;
            {var subQ0=sQuery(id+"F49.wireOp",EDGE,"E306.0.1");Q0=makeQuery(id+"F49.imprint","IMPRINT",FACE,{"disambiguationData":[TD([[makeQuery(id+"F49.imprint","IMPRINT",EDGE,{"derivedFrom":subQ0}),1.0]])]});}
            var Q1;
            {var subQ0=sQuery(id+"F49.wireOp",EDGE,"E305.0.1");Q1=makeQuery(id+"F49.imprint","IMPRINT",FACE,{"disambiguationData":[TD([[makeQuery(id+"F49.imprint","IMPRINT",EDGE,{"derivedFrom":subQ0}),1.0]])]});}
            var Q2;
            {var subQ0=sQuery(id+"F49.wireOp",EDGE,"E304.0.1");Q2=makeQuery(id+"F49.imprint","IMPRINT",FACE,{"disambiguationData":[TD([[makeQuery(id+"F49.imprint","IMPRINT",EDGE,{"derivedFrom":subQ0}),1.0]])]});}
            extrude(context, id + "F50", {"entities" : qUnion([Q0, Q1, Q2]), "operationType" : NewBodyOperationType.ADD, "depth" : 6 * mm});
        }
        {
            var Q0;
            Q0=qCreatedBy(id+"F29.planeOp",FACE);
            var sketch = newSketch(context, id + "F51", { "sketchPlane" : qUnion([Q0])});
            skLineSegment(sketch, "E316.bottom", {"start": v(-1282.5, -307.7) * mm, "end": v(-1168.5, -307.7) * mm});
            skLineSegment(sketch, "E316.top", {"start": v(-1282.5, -170.53) * mm, "end": v(-1168.5, -170.53) * mm});
            skLineSegment(sketch, "E316.left", {"start": v(-1282.5, -307.7) * mm, "end": v(-1282.5, -170.53) * mm});
            skLineSegment(sketch, "E316.right", {"start": v(-1168.5, -307.7) * mm, "end": v(-1168.5, -170.53) * mm});
            skCircle(sketch, "E317", {"center": v(-1171.38, -506.64) * mm, "radius": 74.14 * mm});
            skLineSegment(sketch, "E318.bottom", {"start": v(-1537.94, -415.02) * mm, "end": v(-1351, -415.02) * mm});
            skLineSegment(sketch, "E318.top", {"start": v(-1537.94, -340.13) * mm, "end": v(-1351, -340.13) * mm});
            skLineSegment(sketch, "E318.left", {"start": v(-1537.94, -415.02) * mm, "end": v(-1537.94, -340.13) * mm});
            skLineSegment(sketch, "E318.right", {"start": v(-1351, -415.02) * mm, "end": v(-1351, -340.13) * mm});
            skSolve(sketch);
        }
        {
            var Q0;
            Q0=makeQuery(id+"F51.imprint","IMPRINT",FACE,{"disambiguationData":[TD([[makeQuery(id+"F51.imprint","IMPRINT",EDGE,{"derivedFrom":sQuery(id+"F51.wireOp",EDGE,"E317")}),1.0]])]});
            extrude(context, id + "F52", {"entities" : qUnion([Q0]), "oppositeDirection" : true, "depth" : 123 * mm, "offsetDistance" : 25 * mm});
        }
    });
